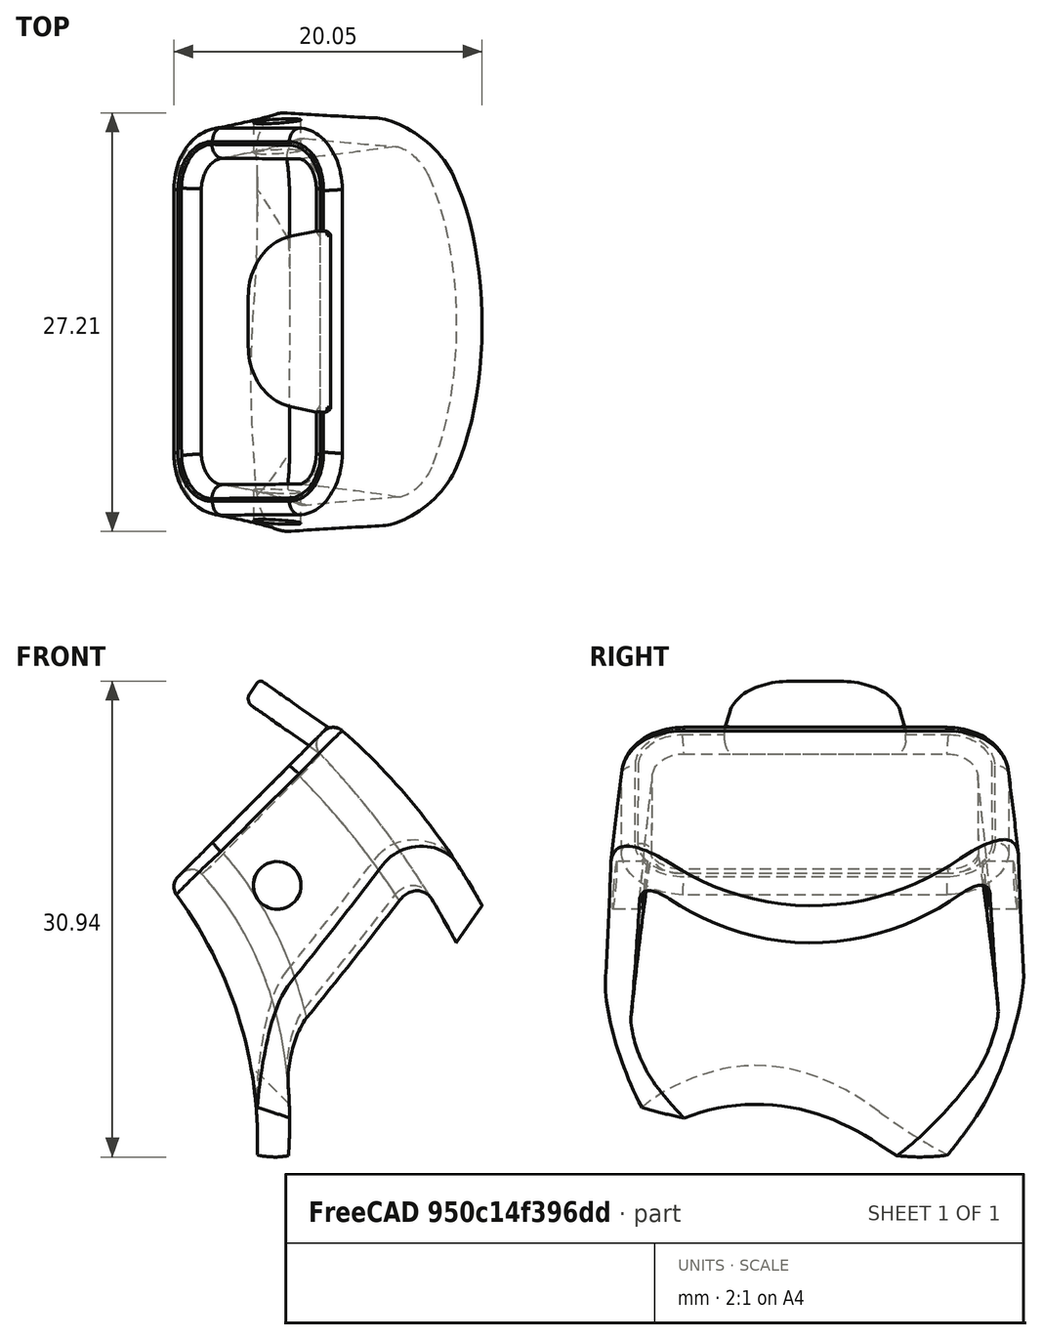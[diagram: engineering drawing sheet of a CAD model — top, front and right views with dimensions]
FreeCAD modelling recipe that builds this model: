
FCSTD DOCUMENT  (FreeCAD 0.20R28671 (Git))
Label: boquilla
License: All rights reserved
LicenseURL: http://en.wikipedia.org/wiki/All_rights_reserved
objects: TechDraw::DrawViewDimension×52, Sketcher::SketchObject×18, TechDraw::DrawViewAnnotation×11, PartDesign::Pocket×7, PartDesign::Plane×6, TechDraw::DrawLeaderLine×6, PartDesign::Fillet×4, TechDraw::DrawViewPart×4, TechDraw::DrawProjGroupItem×3, TechDraw::DrawViewSection×3, PartDesign::Pad×2, TechDraw::DrawViewBalloon×2, PartDesign::AdditivePipe×1, PartDesign::SubtractivePipe×1, TechDraw::DrawSVGTemplate×1, TechDraw::DrawProjGroup×1, TechDraw::DrawViewClip×1, TechDraw::DrawViewSymbol×1, PartDesign::Body×1, TechDraw::DrawPage×1
note: 55 computed .brp shape members not serialized (recipe doc carries the construction recipe); baked Part::Feature solids carry a one-line shape summary decoded from their .brp

FEATURE [Sketcher::SketchObject] Sketch
  FullyConstrained = true
  MapMode = 5
  Placement = pos=(0,0,0) rot=(1,0,0;1.5708rad)
  Support = -> [XZ_Plane]
  sketch-geometry (4):
    g0: ArcOfCircle CenterX=0 CenterY=-24.7487 CenterZ=0 NormalX=0 NormalY=0 NormalZ=1 AngleXU=0 Radius=35 StartAngle=0 EndAngle=0.785398
    g1: LineSegment StartX=35 StartY=-24.7487 StartZ=0 EndX=35 EndY=-62 EndZ=0
    g2: LineSegment StartX=35 StartY=-24.7487 StartZ=0 EndX=0 EndY=-24.7487 EndZ=0
    g3: LineSegment StartX=0 StartY=-24.7487 StartZ=0 EndX=24.7487 EndY=0 EndZ=0
  constraints (11):
    c: Vertical(g1)
    c: Tangent(g1,g0) = 1.5708
    c: Radius(g0) = 35
    c: DistanceY(g1,g0) = 62
    c: Vertical(g0,g-1)
    c: Horizontal(g0,g-1)
    c: Coincident(g2,g0)
    c: Coincident(g2,g0)
    c: Coincident(g3,g0)
    c: Coincident(g3,g0)
    c: Angle(g2,g3) = 0.785398
FEATURE [PartDesign::Plane] DatumPlane
  Length = 66.6467
  MapMode = 7
  Placement = pos=(24.7487,0,-1.5365e-12) rot=(0.678598,0.678598,0.281085;2.59356rad)
  ResizeMode = 0
  Support = -> [Sketch]
  Width = 155.203
FEATURE [Sketcher::SketchObject] Sketch001
  FullyConstrained = true
  MapMode = 5
  Placement = pos=(24.7487,0,-1.5365e-12) rot=(0.678598,0.678598,0.281085;2.59356rad)
  Support = -> [DatumPlane]
  sketch-geometry (10):
    g0: LineSegment StartX=-8.5 StartY=7.5 StartZ=0 EndX=8.5 EndY=7.5 EndZ=0
    g1: LineSegment StartX=12.5 StartY=3.5 StartZ=0 EndX=12.5 EndY=-3.5 EndZ=0
    g2: LineSegment StartX=8.5 StartY=-7.5 StartZ=0 EndX=-8.5 EndY=-7.5 EndZ=0
    g3: LineSegment StartX=-12.5 StartY=-3.5 StartZ=0 EndX=-12.5 EndY=3.5 EndZ=0
    g4: LineSegment StartX=0 StartY=0 StartZ=0 EndX=8.5 EndY=3.5 EndZ=0
    g5: LineSegment StartX=0 StartY=0 StartZ=0 EndX=-8.5 EndY=-3.5 EndZ=0
    g6: ArcOfCircle CenterX=-8.5 CenterY=3.5 CenterZ=0 NormalX=0 NormalY=0 NormalZ=1 AngleXU=0 Radius=4 StartAngle=1.5708 EndAngle=3.14159
    g7: ArcOfCircle CenterX=-8.5 CenterY=-3.5 CenterZ=0 NormalX=0 NormalY=0 NormalZ=1 AngleXU=0 Radius=4 StartAngle=3.14159 EndAngle=4.71239
    g8: ArcOfCircle CenterX=8.5 CenterY=-3.5 CenterZ=0 NormalX=0 NormalY=0 NormalZ=1 AngleXU=0 Radius=4 StartAngle=4.71239 EndAngle=6.28319
    g9: ArcOfCircle CenterX=8.5 CenterY=3.5 CenterZ=0 NormalX=0 NormalY=0 NormalZ=1 AngleXU=0 Radius=4 StartAngle=0 EndAngle=1.5708
  constraints (24):
    c: Horizontal(g0)
    c: Horizontal(g2)
    c: Vertical(g1)
    c: Vertical(g3)
    c: Coincident(g4,g-1)
    c: Coincident(g5,g-1)
    c: Equal(g5,g4)
    c: Tangent(g0,g6) = 1.5708
    c: Tangent(g3,g6) = 1.5708
    c: Tangent(g3,g7) = 1.5708
    c: Tangent(g2,g7) = 1.5708
    c: Tangent(g2,g8) = 1.5708
    c: Tangent(g1,g8) = 1.5708
    c: Tangent(g1,g9) = 1.5708
    c: Tangent(g0,g9) = 1.5708
    c: Coincident(g4,g9)
    c: Coincident(g5,g7)
    c: Equal(g9,g6)
    c: Equal(g6,g7)
    c: Equal(g7,g8)
    c: DistanceY(g2,g0) = 15
    c: DistanceX(g3,g1) = 25
    c: Radius(g7) = 4
    c: Parallel(g4,g5)
FEATURE [PartDesign::Plane] DatumPlane001
  Length = 111.467
  MapMode = 7
  Placement = pos=(35,5.5e-15,-24.7487) rot=(0,0,1;0rad)
  ResizeMode = 0
  Support = -> [Sketch]
  Width = 63.9644
FEATURE [Sketcher::SketchObject] Sketch002
  FullyConstrained = true
  MapMode = 5
  Placement = pos=(35,5.5e-15,-24.7487) rot=(0,0,1;0rad)
  Support = -> [DatumPlane001]
  sketch-geometry (10):
    g0: LineSegment StartX=-6 StartY=15 StartZ=0 EndX=6 EndY=15 EndZ=0
    g1: LineSegment StartX=10 StartY=11 StartZ=0 EndX=10 EndY=-11 EndZ=0
    g2: LineSegment StartX=6 StartY=-15 StartZ=0 EndX=-6 EndY=-15 EndZ=0
    g3: LineSegment StartX=-10 StartY=-11 StartZ=0 EndX=-10 EndY=11 EndZ=0
    g4: ArcOfCircle CenterX=-6 CenterY=11 CenterZ=0 NormalX=0 NormalY=0 NormalZ=1 AngleXU=0 Radius=4 StartAngle=1.5708 EndAngle=3.14159
    g5: ArcOfCircle CenterX=6 CenterY=11 CenterZ=0 NormalX=0 NormalY=0 NormalZ=1 AngleXU=0 Radius=4 StartAngle=0 EndAngle=1.5708
    g6: ArcOfCircle CenterX=-6 CenterY=-11 CenterZ=0 NormalX=0 NormalY=0 NormalZ=1 AngleXU=0 Radius=4 StartAngle=3.14159 EndAngle=4.71239
    g7: ArcOfCircle CenterX=6 CenterY=-11 CenterZ=0 NormalX=0 NormalY=0 NormalZ=1 AngleXU=0 Radius=4 StartAngle=4.71239 EndAngle=6.28319
    g8: LineSegment StartX=-6 StartY=11 StartZ=0 EndX=0 EndY=0 EndZ=0
    g9: LineSegment StartX=0 StartY=0 StartZ=0 EndX=6 EndY=-11 EndZ=0
  constraints (24):
    c: Horizontal(g0)
    c: Horizontal(g2)
    c: Vertical(g1)
    c: Vertical(g3)
    c: Tangent(g0,g4) = 1.5708
    c: Tangent(g3,g4) = 1.5708
    c: Tangent(g0,g5) = 1.5708
    c: Tangent(g1,g5) = 1.5708
    c: Tangent(g3,g6) = 1.5708
    c: Tangent(g2,g6) = 1.5708
    c: Tangent(g2,g7) = 1.5708
    c: Tangent(g1,g7) = 1.5708
    c: Equal(g4,g5)
    c: Equal(g5,g6)
    c: Equal(g6,g7)
    c: Radius(g6) = 4
    c: DistanceX(g3,g1) = 20
    c: DistanceY(g2,g0) = 30
    c: Coincident(g8,g4)
    c: Coincident(g8,g-1)
    c: Coincident(g9,g-1)
    c: Coincident(g9,g7)
    c: Parallel(g9,g8)
    c: Equal(g9,g8)
FEATURE [PartDesign::Plane] DatumPlane002
  Length = 111.467
  MapMode = 7
  Placement = pos=(35,1.38e-14,-62) rot=(0,0,1;0rad)
  ResizeMode = 0
  Support = -> [Sketch]
  Width = 63.9644
FEATURE [Sketcher::SketchObject] Sketch003
  FullyConstrained = true
  MapMode = 5
  Placement = pos=(35,1.38e-14,-62) rot=(0,0,1;0rad)
  Support = -> [DatumPlane002]
  sketch-geometry (10):
    g0: LineSegment StartX=8.5 StartY=17.5 StartZ=0 EndX=-8.5 EndY=17.5 EndZ=0
    g1: LineSegment StartX=-12.5 StartY=13.5 StartZ=0 EndX=-12.5 EndY=-13.5 EndZ=0
    g2: LineSegment StartX=-8.5 StartY=-17.5 StartZ=0 EndX=8.5 EndY=-17.5 EndZ=0
    g3: LineSegment StartX=12.5 StartY=-13.5 StartZ=0 EndX=12.5 EndY=13.5 EndZ=0
    g4: ArcOfCircle CenterX=8.5 CenterY=13.5 CenterZ=0 NormalX=0 NormalY=0 NormalZ=1 AngleXU=0 Radius=4 StartAngle=-7.19e-14 EndAngle=1.5708
    g5: ArcOfCircle CenterX=8.5 CenterY=-13.5 CenterZ=0 NormalX=0 NormalY=0 NormalZ=1 AngleXU=0 Radius=4 StartAngle=4.71239 EndAngle=6.28319
    g6: ArcOfCircle CenterX=-8.5 CenterY=-13.5 CenterZ=0 NormalX=0 NormalY=0 NormalZ=1 AngleXU=0 Radius=4 StartAngle=3.14159 EndAngle=4.71239
    g7: ArcOfCircle CenterX=-8.5 CenterY=13.5 CenterZ=0 NormalX=0 NormalY=0 NormalZ=1 AngleXU=0 Radius=4 StartAngle=1.5708 EndAngle=3.14159
    g8: LineSegment StartX=-8.5 StartY=13.5 StartZ=0 EndX=0 EndY=0 EndZ=0
    g9: LineSegment StartX=0 StartY=0 StartZ=0 EndX=8.5 EndY=-13.5 EndZ=0
  constraints (24):
    c: Horizontal(g0)
    c: Horizontal(g2)
    c: Vertical(g1)
    c: Vertical(g3)
    c: Tangent(g3,g4) = -1.5708
    c: Tangent(g0,g4) = -1.5708
    c: Tangent(g3,g5) = -1.5708
    c: Tangent(g2,g5) = -1.5708
    c: Tangent(g2,g6) = -1.5708
    c: Tangent(g1,g6) = -1.5708
    c: Tangent(g1,g7) = -1.5708
    c: Tangent(g0,g7) = -1.5708
    c: Equal(g5,g4)
    c: Equal(g4,g7)
    c: Equal(g7,g6)
    c: Radius(g6) = 4
    c: DistanceX(g1,g3) = 25
    c: DistanceY(g2,g0) = 35
    c: Coincident(g8,g7)
    c: Coincident(g8,g-1)
    c: Coincident(g9,g-1)
    c: Coincident(g9,g5)
    c: Equal(g8,g9)
    c: Parallel(g9,g8)
FEATURE [PartDesign::AdditivePipe] AdditivePipe
  AuxilleryCurvelinear = true
  AuxillerySpineTangent = false
  Binormal = (0,0,0)
  Mode = 0
  Placement = pos=(24.7487,0,-1.537e-12) rot=(0.678598,0.678598,0.281085;2.59356rad)
  Profile = -> Sketch001
  Sections = -> [Sketch002,Sketch003]
  Spine = -> Sketch
  SpineTangent = false
  Transformation = 1
  Transition = 0
FEATURE [Sketcher::SketchObject] Sketch004
  ExternalGeometry = -> [AdditivePipe]
  FullyConstrained = true
  MapMode = 5
  Placement = pos=(24.7487,-8.1e-15,-62) rot=(0.707107,0.707107,0;3.14159rad)
  Support = -> [AdditivePipe]
  sketch-geometry (24):
    g0: LineSegment StartX=-13.5 StartY=22.7513 StartZ=0 EndX=13.5 EndY=-2.24874 EndZ=0
    g1: LineSegment StartX=13.5 StartY=22.7513 StartZ=0 EndX=-13.5 EndY=-2.24874 EndZ=0
    g2: GeomPoint X=2.51e-14 Y=10.2513 Z=0
    g3: LineSegment StartX=-12.5 StartY=20.7513 StartZ=0 EndX=12.5 EndY=20.7513 EndZ=0
    g4: LineSegment StartX=15.5 StartY=17.7513 StartZ=0 EndX=15.5 EndY=5 EndZ=0
    g5: LineSegment StartX=12.5 StartY=2 StartZ=0 EndX=-12.5 EndY=2 EndZ=0
    g6: LineSegment StartX=-15.5 StartY=5 StartZ=0 EndX=-15.5 EndY=17.7513 EndZ=0
    g7: ArcOfCircle CenterX=-12.5 CenterY=17.7513 CenterZ=0 NormalX=0 NormalY=0 NormalZ=1 AngleXU=0 Radius=3 StartAngle=1.5708 EndAngle=3.14159
    g8: ArcOfCircle CenterX=12.5 CenterY=17.7513 CenterZ=0 NormalX=0 NormalY=0 NormalZ=1 AngleXU=0 Radius=3 StartAngle=2e-16 EndAngle=1.5708
    g9: ArcOfCircle CenterX=12.5 CenterY=5 CenterZ=0 NormalX=0 NormalY=0 NormalZ=1 AngleXU=0 Radius=3 StartAngle=4.71239 EndAngle=6.28319
    g10: ArcOfCircle CenterX=-12.5 CenterY=5 CenterZ=0 NormalX=0 NormalY=0 NormalZ=1 AngleXU=0 Radius=3 StartAngle=3.14159 EndAngle=4.71239
    g11: LineSegment StartX=-12.5 StartY=20.7513 StartZ=0 EndX=-12.5 EndY=22.7513 EndZ=0
    g12: LineSegment StartX=-12.5 StartY=2 StartZ=0 EndX=-12.5 EndY=0 EndZ=0
    g13: LineSegment StartX=-15.5 StartY=5 StartZ=0 EndX=-17.5 EndY=5 EndZ=0
    g14: LineSegment StartX=15.5 StartY=5 StartZ=0 EndX=17.5 EndY=5 EndZ=0
    g15: LineSegment StartX=-19.5 StartY=24.7513 StartZ=0 EndX=19.5 EndY=24.7513 EndZ=0
    g16: LineSegment StartX=19.5 StartY=24.7513 StartZ=0 EndX=19.5 EndY=-4.24874 EndZ=0
    g17: LineSegment StartX=19.5 StartY=-4.24874 StartZ=0 EndX=-19.5 EndY=-4.24874 EndZ=0
    g18: LineSegment StartX=-19.5 StartY=-4.24874 StartZ=0 EndX=-19.5 EndY=24.7513 EndZ=0
    g19: LineSegment StartX=-19.5 StartY=24.7513 StartZ=0 EndX=-17.5 EndY=18.7513 EndZ=0
    g20: LineSegment StartX=-19.5 StartY=24.7513 StartZ=0 EndX=-13.5 EndY=22.7513 EndZ=0
    g21: LineSegment StartX=19.5 StartY=-4.24874 StartZ=0 EndX=13.5 EndY=-2.24874 EndZ=0
    g22: LineSegment StartX=19.5 StartY=-4.24874 StartZ=0 EndX=17.5 EndY=1.75126 EndZ=0
    g23: LineSegment StartX=17.5 StartY=18.7513 StartZ=0 EndX=19.5 EndY=18.7513 EndZ=0
  constraints (61):
    c: Coincident(g0,g-3)
    c: Coincident(g0,g-4)
    c: Coincident(g1,g-5)
    c: Coincident(g1,g-6)
    c: PointOnObject(g2,g0)
    c: PointOnObject(g2,g1)
    c: Horizontal(g3)
    c: Horizontal(g5)
    c: Vertical(g4)
    c: Vertical(g6)
    c: Tangent(g3,g7) = 1.5708
    c: Tangent(g6,g7) = 1.5708
    c: Tangent(g3,g8) = 1.5708
    c: Tangent(g4,g8) = 1.5708
    c: Tangent(g4,g9) = 1.5708
    c: Tangent(g5,g9) = 1.5708
    c: Tangent(g5,g10) = 1.5708
    c: Tangent(g6,g10) = 1.5708
    c: Equal(g7,g8)
    c: Equal(g8,g10)
    c: Equal(g10,g9)
    c: Radius(g9) = 3
    c: DistanceY(g3,g1) = 2
    c: Coincident(g11,g3)
    c: Vertical(g11)
    c: Horizontal(g11,g0)
    c: Coincident(g12,g5)
    c: PointOnObject(g12,g-1)
    c: Vertical(g12)
    c: Equal(g12,g11)
    c: Coincident(g13,g6)
    c: Horizontal(g13)
    c: Coincident(g14,g4)
    c: Horizontal(g14)
    c: Vertical(g-6,g13)
    c: Vertical(g-4,g14)
    c: Equal(g12,g13)
    c: Equal(g13,g14)
    c: Coincident(g15,g16)
    c: Coincident(g16,g17)
    c: Coincident(g17,g18)
    c: Coincident(g18,g15)
    c: Horizontal(g15)
    c: Horizontal(g17)
    c: Vertical(g16)
    c: Vertical(g18)
    c: Coincident(g19,g15)
    c: Coincident(g19,g-3)
    c: Coincident(g20,g15)
    c: Coincident(g20,g0)
    c: Coincident(g21,g16)
    c: Coincident(g21,g0)
    c: Coincident(g22,g16)
    c: Coincident(g22,g-4)
    c: Equal(g22,g21)
    c: Equal(g21,g19)
    c: Equal(g19,g20)
    c: Coincident(g23,g-5)
    c: PointOnObject(g23,g16)
    c: Horizontal(g23)
    c: Equal(g11,g23)
FEATURE [PartDesign::Pocket] Pocket
  BaseFeature = -> AdditivePipe
  Direction = (-1e-16,0,1)
  Length = 2
  Length2 = 100
  Placement = pos=(24.7487,0,-1.537e-12) rot=(0.678598,0.678598,0.281085;2.59356rad)
  Profile = -> Sketch004
  Type = 0
FEATURE [Sketcher::SketchObject] Sketch006
  FullyConstrained = true
  MapMode = 5
  Placement = pos=(24.7487,0,-1.5365e-12) rot=(0.678598,0.678598,0.281085;2.59356rad)
  Support = -> [DatumPlane]
  sketch-geometry (10):
    g0: LineSegment StartX=-8.5 StartY=5.5 StartZ=0 EndX=8.5 EndY=5.5 EndZ=0
    g1: LineSegment StartX=10.5 StartY=3.5 StartZ=0 EndX=10.5 EndY=-3.5 EndZ=0
    g2: LineSegment StartX=8.5 StartY=-5.5 StartZ=0 EndX=-8.5 EndY=-5.5 EndZ=0
    g3: LineSegment StartX=-10.5 StartY=-3.5 StartZ=0 EndX=-10.5 EndY=3.5 EndZ=0
    g4: ArcOfCircle CenterX=-8.5 CenterY=3.5 CenterZ=0 NormalX=0 NormalY=0 NormalZ=1 AngleXU=0 Radius=2 StartAngle=1.5708 EndAngle=3.14159
    g5: ArcOfCircle CenterX=-8.5 CenterY=-3.5 CenterZ=0 NormalX=0 NormalY=0 NormalZ=1 AngleXU=0 Radius=2 StartAngle=3.14159 EndAngle=4.71239
    g6: ArcOfCircle CenterX=8.5 CenterY=-3.5 CenterZ=0 NormalX=0 NormalY=0 NormalZ=1 AngleXU=0 Radius=2 StartAngle=4.71239 EndAngle=6.28319
    g7: ArcOfCircle CenterX=8.5 CenterY=3.5 CenterZ=0 NormalX=0 NormalY=0 NormalZ=1 AngleXU=0 Radius=2 StartAngle=0 EndAngle=1.5708
    g8: LineSegment StartX=-8.5 StartY=3.5 StartZ=0 EndX=0 EndY=0 EndZ=0
    g9: LineSegment StartX=0 StartY=0 StartZ=0 EndX=8.5 EndY=-3.5 EndZ=0
  constraints (24):
    c: Horizontal(g0)
    c: Horizontal(g2)
    c: Vertical(g1)
    c: Vertical(g3)
    c: Tangent(g0,g4) = 1.5708
    c: Tangent(g3,g4) = 1.5708
    c: Tangent(g3,g5) = 1.5708
    c: Tangent(g2,g5) = 1.5708
    c: Tangent(g2,g6) = 1.5708
    c: Tangent(g1,g6) = 1.5708
    c: Tangent(g1,g7) = 1.5708
    c: Tangent(g0,g7) = 1.5708
    c: Equal(g4,g5)
    c: Equal(g5,g6)
    c: Equal(g6,g7)
    c: Radius(g4) = 2
    c: Coincident(g8,g4)
    c: Coincident(g8,g-1)
    c: Coincident(g9,g-1)
    c: Coincident(g9,g6)
    c: Equal(g9,g8)
    c: Parallel(g8,g9)
    c: DistanceY(g2,g0) = 11
    c: DistanceX(g3,g1) = 21
FEATURE [Sketcher::SketchObject] Sketch007
  FullyConstrained = true
  MapMode = 5
  Placement = pos=(35,5.5e-15,-24.7487) rot=(0,0,1;0rad)
  Support = -> [DatumPlane001]
  sketch-geometry (10):
    g0: LineSegment StartX=-6 StartY=13 StartZ=0 EndX=6 EndY=13 EndZ=0
    g1: LineSegment StartX=8 StartY=11 StartZ=0 EndX=8 EndY=-11 EndZ=0
    g2: LineSegment StartX=6 StartY=-13 StartZ=0 EndX=-6 EndY=-13 EndZ=0
    g3: LineSegment StartX=-8 StartY=-11 StartZ=0 EndX=-8 EndY=11 EndZ=0
    g4: ArcOfCircle CenterX=6 CenterY=11 CenterZ=0 NormalX=0 NormalY=0 NormalZ=1 AngleXU=0 Radius=2 StartAngle=8.55e-14 EndAngle=1.5708
    g5: ArcOfCircle CenterX=-6 CenterY=11 CenterZ=0 NormalX=0 NormalY=0 NormalZ=1 AngleXU=0 Radius=2 StartAngle=1.5708 EndAngle=3.14159
    g6: ArcOfCircle CenterX=-6 CenterY=-11 CenterZ=0 NormalX=0 NormalY=0 NormalZ=1 AngleXU=0 Radius=2 StartAngle=3.14159 EndAngle=4.71239
    g7: ArcOfCircle CenterX=6 CenterY=-11 CenterZ=0 NormalX=0 NormalY=0 NormalZ=1 AngleXU=0 Radius=2 StartAngle=4.71239 EndAngle=6.28319
    g8: LineSegment StartX=-6 StartY=11 StartZ=0 EndX=0 EndY=0 EndZ=0
    g9: LineSegment StartX=0 StartY=0 StartZ=0 EndX=6 EndY=-11 EndZ=0
  constraints (24):
    c: Horizontal(g0)
    c: Horizontal(g2)
    c: Vertical(g1)
    c: Vertical(g3)
    c: Tangent(g1,g4) = 1.5708
    c: Tangent(g0,g4) = 1.5708
    c: Tangent(g0,g5) = 1.5708
    c: Tangent(g3,g5) = 1.5708
    c: Tangent(g3,g6) = 1.5708
    c: Tangent(g2,g6) = 1.5708
    c: Tangent(g2,g7) = 1.5708
    c: Tangent(g1,g7) = 1.5708
    c: Equal(g4,g5)
    c: Equal(g5,g6)
    c: Equal(g6,g7)
    c: Radius(g4) = 2
    c: Coincident(g8,g5)
    c: Coincident(g8,g-1)
    c: Coincident(g9,g-1)
    c: Coincident(g9,g7)
    c: Equal(g8,g9)
    c: Parallel(g8,g9)
    c: DistanceX(g3,g1) = 16
    c: DistanceY(g2,g0) = 26
FEATURE [PartDesign::Plane] DatumPlane003
  AttachmentOffset = pos=(0,0,-2) rot=(0,0,1;0rad)
  Length = 63.9644
  MapMode = 5
  Placement = pos=(24.7487,0,-58) rot=(0.707107,0.707107,0;3.14159rad)
  ResizeMode = 0
  Support = -> [Pocket]
  Width = 111.467
FEATURE [Sketcher::SketchObject] Sketch008
  ExternalGeometry = -> [Sketch]
  FullyConstrained = true
  MapMode = 5
  Placement = pos=(24.7487,0,-58) rot=(0.707107,0.707107,0;3.14159rad)
  Support = -> [DatumPlane003]
  sketch-geometry (10):
    g0: LineSegment StartX=-13.5 StartY=20.7513 StartZ=0 EndX=13.5 EndY=20.7513 EndZ=0
    g1: LineSegment StartX=15.5 StartY=18.7513 StartZ=0 EndX=15.5 EndY=1.75126 EndZ=0
    g2: LineSegment StartX=13.5 StartY=-0.248737 StartZ=0 EndX=-13.5 EndY=-0.248737 EndZ=0
    g3: LineSegment StartX=-15.5 StartY=1.75126 StartZ=0 EndX=-15.5 EndY=18.7513 EndZ=0
    g4: ArcOfCircle CenterX=-13.5 CenterY=18.7513 CenterZ=0 NormalX=0 NormalY=0 NormalZ=1 AngleXU=0 Radius=2 StartAngle=1.5708 EndAngle=3.14159
    g5: ArcOfCircle CenterX=13.5 CenterY=18.7513 CenterZ=0 NormalX=0 NormalY=0 NormalZ=1 AngleXU=0 Radius=2 StartAngle=8.58e-14 EndAngle=1.5708
    g6: ArcOfCircle CenterX=13.5 CenterY=1.75126 CenterZ=0 NormalX=0 NormalY=0 NormalZ=1 AngleXU=0 Radius=2 StartAngle=4.71239 EndAngle=6.28319
    g7: ArcOfCircle CenterX=-13.5 CenterY=1.75126 CenterZ=0 NormalX=0 NormalY=0 NormalZ=1 AngleXU=0 Radius=2 StartAngle=3.14159 EndAngle=4.71239
    g8: LineSegment StartX=-13.5 StartY=18.7513 StartZ=0 EndX=3.55e-14 EndY=10.2513 EndZ=0
    g9: LineSegment StartX=3.55e-14 StartY=10.2513 StartZ=0 EndX=13.5 EndY=1.75126 EndZ=0
  constraints (24):
    c: Horizontal(g0)
    c: Horizontal(g2)
    c: Vertical(g1)
    c: Vertical(g3)
    c: Tangent(g0,g4) = 1.5708
    c: Tangent(g3,g4) = 1.5708
    c: Tangent(g0,g5) = 1.5708
    c: Tangent(g1,g5) = 1.5708
    c: Tangent(g1,g6) = 1.5708
    c: Tangent(g2,g6) = 1.5708
    c: Tangent(g2,g7) = 1.5708
    c: Tangent(g3,g7) = 1.5708
    c: Equal(g6,g5)
    c: Equal(g5,g4)
    c: Equal(g4,g7)
    c: Radius(g5) = 2
    c: Coincident(g8,g4)
    c: Coincident(g8,g-3)
    c: Coincident(g9,g8)
    c: Coincident(g9,g6)
    c: Parallel(g9,g8)
    c: Equal(g9,g8)
    c: DistanceX(g3,g1) = 31
    c: DistanceY(g2,g0) = 21
FEATURE [Sketcher::SketchObject] Sketch009
  ExternalGeometry = -> [Sketch,Sketch008]
  FullyConstrained = true
  MapMode = 5
  Placement = pos=(0,0,0) rot=(1,0,0;1.5708rad)
  Support = -> [XZ_Plane]
  sketch-geometry (2):
    g0: ArcOfCircle CenterX=3.3e-15 CenterY=-24.7487 CenterZ=0 NormalX=0 NormalY=0 NormalZ=1 AngleXU=0 Radius=35 StartAngle=0 EndAngle=0.785398
    g1: LineSegment StartX=35 StartY=-24.7487 StartZ=0 EndX=35 EndY=-58 EndZ=0
  constraints (6):
    c: Coincident(g0,g-3)
    c: Coincident(g0,g-4)
    c: Tangent(g0,g-3)
    c: Coincident(g1,g0)
    c: PointOnObject(g1,g-4)
    c: Horizontal(g1,g-5)
FEATURE [PartDesign::SubtractivePipe] SubtractivePipe
  AuxilleryCurvelinear = true
  AuxillerySpineTangent = false
  BaseFeature = -> Pocket
  Binormal = (0,0,0)
  Mode = 1
  Placement = pos=(24.7487,0,-1.537e-12) rot=(0.678598,0.678598,0.281085;2.59356rad)
  Profile = -> Sketch006
  Sections = -> [Sketch007,Sketch008]
  Spine = -> Sketch009
  SpineTangent = false
  Transformation = 1
  Transition = 0
FEATURE [PartDesign::Plane] DatumPlane004
  AttachmentOffset = pos=(0,0,35) rot=(0,0,1;0rad)
  Length = 64.0318
  MapMode = 5
  Placement = pos=(35,-7.8e-15,7.8e-15) rot=(0.57735,0.57735,0.57735;2.0944rad)
  ResizeMode = 0
  Support = -> [YZ_Plane]
  Width = 112.478
FEATURE [Sketcher::SketchObject] Sketch010
  ExternalGeometry = -> [Sketch008]
  FullyConstrained = true
  MapMode = 5
  Placement = pos=(35,-7.8e-15,7.8e-15) rot=(0.57735,0.57735,0.57735;2.0944rad)
  Support = -> [DatumPlane004]
  sketch-geometry (6):
    g0: LineSegment StartX=-9.4 StartY=-58 StartZ=0 EndX=9.4 EndY=-58 EndZ=0
    g1: LineSegment StartX=9.4 StartY=-58 StartZ=0 EndX=9.4 EndY=-29.5 EndZ=0
    g2: LineSegment StartX=9.4 StartY=-29.5 StartZ=0 EndX=-9.4 EndY=-29.5 EndZ=0
    g3: LineSegment StartX=-9.4 StartY=-29.5 StartZ=0 EndX=-9.4 EndY=-58 EndZ=0
    g4: LineSegment StartX=-13.5 StartY=-58 StartZ=0 EndX=-9.4 EndY=-58 EndZ=0
    g5: LineSegment StartX=13.5 StartY=-58 StartZ=0 EndX=9.4 EndY=-58 EndZ=0
  constraints (16):
    c: Coincident(g0,g1)
    c: Coincident(g1,g2)
    c: Coincident(g2,g3)
    c: Coincident(g3,g0)
    c: Horizontal(g0)
    c: Horizontal(g2)
    c: Vertical(g1)
    c: Vertical(g3)
    c: PointOnObject(g0,g-3)
    c: DistanceX(g0,g0) = 18.8
    c: DistanceY(g0,g1) = 28.5
    c: Coincident(g4,g-3)
    c: Coincident(g5,g-3)
    c: Equal(g5,g4)
    c: Coincident(g4,g0)
    c: Coincident(g5,g0)
FEATURE [PartDesign::Pocket] Pocket001
  BaseFeature = -> SubtractivePipe
  Direction = (-1,1e-16,-1e-16)
  Length = 5
  Length2 = 100
  Placement = pos=(24.7487,0,-1.537e-12) rot=(0.678598,0.678598,0.281085;2.59356rad)
  Profile = -> Sketch010
  Reversed = true
  Type = 1
FEATURE [Sketcher::SketchObject] Sketch011
  ExternalGeometry = -> [Pocket001]
  FullyConstrained = true
  MapMode = 5
  Placement = pos=(0,0,0) rot=(1,0,0;1.5708rad)
  Support = -> [XZ_Plane]
  sketch-geometry (1):
    g0: Circle CenterX=26.4454 CenterY=-5.3033 CenterZ=0 NormalX=0 NormalY=0 NormalZ=1 AngleXU=0 Radius=1.55
  constraints (3):
    c: Diameter(g0) = 3.1
    c: DistanceX(g-3,g0) = 7
    c: DistanceY(g0,g-3) = 0
FEATURE [PartDesign::Pocket] Pocket002
  BaseFeature = -> Pocket001
  Direction = (0,1,2e-16)
  Length = 5
  Length2 = 100
  Midplane = true
  Placement = pos=(24.7487,0,-1.537e-12) rot=(0.678598,0.678598,0.281085;2.59356rad)
  Profile = -> Sketch011
  Type = 1
FEATURE [PartDesign::Fillet] Fillet
  Base = -> Pocket002 [Edge79,Edge87]
  BaseFeature = -> Pocket002
  Placement = pos=(24.7487,0,-1.537e-12) rot=(0.678598,0.678598,0.281085;2.59356rad)
  Radius = 0.9
  SupportTransform = false
  UseAllEdges = false
FEATURE [Sketcher::SketchObject] Sketch012
  ExternalGeometry = -> [Sketch,Fillet]
  FullyConstrained = true
  MapMode = 5
  Placement = pos=(0,0,0) rot=(1,0,0;1.5708rad)
  Support = -> [XZ_Plane]
  sketch-geometry (1):
    g0: LineSegment StartX=29.2448 StartY=3.25778 StartZ=0 EndX=0 EndY=23.7352 EndZ=0
  constraints (3):
    c: Angle(g0,g-3) = 2.18166
    c: Vertical(g-1,g0)
    c: Coincident(g0,g-6)
FEATURE [PartDesign::Plane] DatumPlane005
  Length = 66.5128
  MapMode = 13
  Placement = pos=(19.4965,2.85578,10.0836) rot=(0.287968,0.287968,0.913318;1.66134rad)
  ResizeMode = 0
  Support = -> [Sketch012,Fillet]
  Width = 152.849
FEATURE [Sketcher::SketchObject] Sketch013
  ExternalGeometry = -> [Sketch012]
  FullyConstrained = true
  MapMode = 5
  Placement = pos=(19.4965,2.85578,10.0836) rot=(0.287968,0.287968,0.913318;1.66134rad)
  Support = -> [DatumPlane005]
  sketch-geometry (6):
    g0: LineSegment StartX=-8.85578 StartY=-11.9004 StartZ=0 EndX=-7.85578 EndY=-5.90042 EndZ=0
    g1: LineSegment StartX=-7.85578 StartY=-5.90042 StartZ=0 EndX=2.14422 EndY=-5.90042 EndZ=0
    g2: LineSegment StartX=2.14422 StartY=-5.90042 StartZ=0 EndX=3.14422 EndY=-11.9004 EndZ=0
    g3: LineSegment StartX=-8.85578 StartY=-11.9004 StartZ=0 EndX=3.14422 EndY=-11.9004 EndZ=0
    g4: LineSegment StartX=-2.85578 StartY=-11.9004 StartZ=0 EndX=-8.85578 EndY=-11.9004 EndZ=0
    g5: LineSegment StartX=-2.85578 StartY=-11.9004 StartZ=0 EndX=3.14422 EndY=-11.9004 EndZ=0
  constraints (16):
    c: Coincident(g1,g0)
    c: Horizontal(g1)
    c: Coincident(g2,g1)
    c: Coincident(g3,g0)
    c: Coincident(g3,g2)
    c: Horizontal(g3)
    c: Equal(g4,g5)
    c: Coincident(g4,g0)
    c: Coincident(g5,g2)
    c: Equal(g0,g2)
    c: DistanceY(g2,g1) = 6
    c: DistanceX(g3,g3) = 12
    c: DistanceX(g1,g1) = 10
    c: Coincident(g5,g4)
    c: Horizontal(g5)
    c: Coincident(g4,g-3)
FEATURE [PartDesign::Pad] Pad
  BaseFeature = -> Fillet
  Direction = (0.573576,1.4e-15,0.819152)
  Length = 1.7
  Length2 = 100
  Placement = pos=(24.7487,0,-1.537e-12) rot=(0.678598,0.678598,0.281085;2.59356rad)
  Profile = -> Sketch013
  ReferenceAxis = -> Sketch013 [N_Axis]
  Type = 0
FEATURE [PartDesign::Fillet] Fillet001
  Base = -> Pad [Edge104,Edge85]
  BaseFeature = -> Pad
  Placement = pos=(24.7487,0,-1.537e-12) rot=(0.678598,0.678598,0.281085;2.59356rad)
  Radius = 4
  SupportTransform = false
  UseAllEdges = false
FEATURE [PartDesign::Fillet] Fillet002
  Base = -> Fillet001 [Edge1,Edge7,Edge11,Edge10,Edge8]
  BaseFeature = -> Fillet001
  Placement = pos=(24.7487,0,-1.537e-12) rot=(0.678598,0.678598,0.281085;2.59356rad)
  Radius = 0.6
  SupportTransform = false
  UseAllEdges = false
FEATURE [PartDesign::Fillet] Fillet003
  Base = -> Fillet002 [Face4]
  BaseFeature = -> Fillet002
  Placement = pos=(24.7487,0,-1.537e-12) rot=(0.678598,0.678598,0.281085;2.59356rad)
  Radius = 0.3
  SupportTransform = false
  UseAllEdges = false
FEATURE [Sketcher::SketchObject] Sketch014
  ExternalGeometry = -> [Fillet003]
  FullyConstrained = true
  MapMode = 5
  Placement = pos=(24.7487,-8.1e-15,-62) rot=(0.707107,0.707107,0;3.14159rad)
  Support = -> [Fillet003]
  sketch-geometry (1):
    g0: Circle CenterX=-8.5 CenterY=7 CenterZ=0 NormalX=0 NormalY=0 NormalZ=1 AngleXU=0 Radius=2.5
  constraints (3):
    c: Diameter(g0) = 5
    c: DistanceX(g-4,g0) = 4
    c: DistanceY(g-4,g0) = 5
FEATURE [PartDesign::Pocket] Pocket003
  BaseFeature = -> Fillet003
  Direction = (-7e-16,1e-16,1)
  Length = 0
  Length2 = 100
  Placement = pos=(24.7487,0,-1.537e-12) rot=(0.678598,0.678598,0.281085;2.59356rad)
  Profile = -> Sketch014
  Type = 3
  UpToFace = -> Fillet003 [Face65]
FEATURE [Sketcher::SketchObject] Sketch015
  ExternalGeometry = -> [Pocket003]
  FullyConstrained = true
  MapMode = 5
  Placement = pos=(35,-7.8e-15,7.8e-15) rot=(0.57735,0.57735,0.57735;2.0944rad)
  Support = -> [DatumPlane004]
  sketch-geometry (1):
    g0: Circle CenterX=0 CenterY=-44 CenterZ=0 NormalX=0 NormalY=0 NormalZ=1 AngleXU=0 Radius=5
  constraints (3):
    c: PointOnObject(g0,g-2)
    c: Diameter(g0) = 10
    c: DistanceY(g-3,g0) = 18
FEATURE [PartDesign::Pocket] Pocket004
  BaseFeature = -> Pocket003
  Direction = (-1,1e-16,-1e-16)
  Length = 5
  Length2 = 100
  Placement = pos=(24.7487,0,-1.537e-12) rot=(0.678598,0.678598,0.281085;2.59356rad)
  Profile = -> Sketch015
  Type = 1
FEATURE [Sketcher::SketchObject] Sketch016
  ExternalGeometry = -> [Pocket004]
  FullyConstrained = true
  MapMode = 5
  Placement = pos=(24.7487,-8.1e-15,-62) rot=(0.707107,0.707107,0;3.14159rad)
  Support = -> [Pocket004]
  sketch-geometry (9):
    g0: ArcOfCircle CenterX=-12.5 CenterY=17.7513 CenterZ=0 NormalX=0 NormalY=0 NormalZ=1 AngleXU=0 Radius=3 StartAngle=1.5708 EndAngle=3.14159
    g1: ArcOfCircle CenterX=12.5 CenterY=17.7513 CenterZ=0 NormalX=0 NormalY=0 NormalZ=1 AngleXU=0 Radius=3 StartAngle=8e-16 EndAngle=1.5708
    g2: ArcOfCircle CenterX=12.5 CenterY=5 CenterZ=0 NormalX=0 NormalY=0 NormalZ=1 AngleXU=0 Radius=3 StartAngle=4.71239 EndAngle=6.28319
    g3: ArcOfCircle CenterX=-12.5 CenterY=5 CenterZ=0 NormalX=0 NormalY=0 NormalZ=1 AngleXU=0 Radius=3 StartAngle=3.14159 EndAngle=4.71239
    g4: LineSegment StartX=-15.5 StartY=17.7513 StartZ=0 EndX=-15.5 EndY=5 EndZ=0
    g5: LineSegment StartX=-12.5 StartY=2 StartZ=0 EndX=12.5 EndY=2 EndZ=0
    g6: LineSegment StartX=15.5 StartY=5 StartZ=0 EndX=15.5 EndY=17.7513 EndZ=0
    g7: LineSegment StartX=12.5 StartY=20.7513 StartZ=0 EndX=-12.5 EndY=20.7513 EndZ=0
    g8: Circle CenterX=-8.5 CenterY=7 CenterZ=0 NormalX=0 NormalY=0 NormalZ=1 AngleXU=0 Radius=2.5
  constraints (18):
    c: Coincident(g4,g3)
    c: Coincident(g6,g2)
    c: Coincident(g7,g1)
    c: Coincident(g7,g0)
    c: Tangent(g4,g0) = -1.5708
    c: Tangent(g6,g1) = -1.5708
    c: Tangent(g5,g2) = -1.5708
    c: Tangent(g5,g3) = -1.5708
    c: Coincident(g-10,g3)
    c: Coincident(g-10,g2)
    c: Coincident(g-4,g2)
    c: Coincident(g-9,g3)
    c: Coincident(g-5,g1)
    c: Coincident(g0,g-8)
    c: Coincident(g0,g-7)
    c: Coincident(g1,g-6)
    c: Coincident(g-11,g8)
    c: Equal(g-11,g8)
FEATURE [PartDesign::Pad] Pad001
  BaseFeature = -> Pocket004
  Direction = (9e-16,-1e-16,-1)
  Length = 2
  Length2 = 10
  Placement = pos=(24.7487,0,-1.537e-12) rot=(0.678598,0.678598,0.281085;2.59356rad)
  Profile = -> Sketch016
  ReferenceAxis = -> Sketch016 [N_Axis]
  Type = 0
FEATURE [TechDraw::DrawSVGTemplate] Template003
  EditableTexts = AUTHOR_NAME=Daniel García García; DATE=14-04-2022; DN=10; DOCUMENT_TYPE=Plano de pieza; PN=13; REVISION=1; SCALE=1:1; SHEET=10/15; SIZE=A4; TITLELINE-1=Boquilla
  Height = 210
  Orientation = 1
  Width = 297
FEATURE [TechDraw::DrawProjGroupItem] ProjItem  label="Front"
  CoarseView = false
  Direction = (-1,0,0)
  Focus = 100
  HardHidden = false
  IsoCount = 0
  IsoHidden = false
  IsoVisible = false
  LockPosition = true
  Perspective = false
  Rotation = 0
  RotationVector = (0,-1,0)
  ScaleType = 2
  SeamHidden = false
  SeamVisible = true
  SmoothHidden = false
  SmoothVisible = true
  Source = -> [Pad001]
  Type = 0
  X = 0
  XDirection = (0,-1,0)
  Y = 0
FEATURE [TechDraw::DrawProjGroupItem] ProjItem001  label="Right"
  CoarseView = false
  Direction = (-1e-16,-1,0)
  Focus = 100
  HardHidden = false
  IsoCount = 0
  IsoHidden = false
  IsoVisible = false
  LockPosition = true
  Perspective = false
  Rotation = 0
  RotationVector = (1,0,0)
  ScaleType = 2
  SeamHidden = false
  SeamVisible = true
  SmoothHidden = false
  SmoothVisible = true
  Source = -> [Pad001]
  Type = 2
  X = -98.1887
  XDirection = (1,-1e-16,0)
  Y = 0
FEATURE [TechDraw::DrawProjGroupItem] ProjItem002  label="Rear"
  CoarseView = false
  Direction = (1,0,0)
  Focus = 100
  HardHidden = false
  IsoCount = 0
  IsoHidden = false
  IsoVisible = false
  LockPosition = true
  Perspective = false
  Rotation = 0
  RotationVector = (1,0,0)
  ScaleType = 2
  SeamHidden = false
  SeamVisible = true
  SmoothHidden = false
  SmoothVisible = true
  Source = -> [Pad001]
  Type = 3
  X = 83.712
  XDirection = (0,1,0)
  Y = 0
FEATURE [TechDraw::DrawProjGroup] ProjGroup
  Anchor = -> ProjItem
  AutoDistribute = true
  LockPosition = false
  ProjectionType = 0
  Rotation = 0
  ScaleType = 0
  Source = -> [Pad001,Sketch003]
  Views = -> [ProjItem,ProjItem001,ProjItem002]
  X = 164.554
  Y = 125.603
  spacingX = 15
  spacingY = 15
FEATURE [TechDraw::DrawViewDimension] Dimension
  AngleOverride = false
  Arbitrary = false
  ArbitraryTolerances = false
  EqualTolerance = true
  ExtensionAngle = 0
  FormatSpec = ⌀%.2w
  FormatSpecOverTolerance = %+.2w
  FormatSpecUnderTolerance = %+.2w
  Inverted = false
  LineAngle = 0
  LockPosition = false
  MeasureType = 1
  OverTolerance = 0
  References2D = -> [ProjItem]
  Rotation = 0
  ScaleType = 0
  TheoreticalExact = false
  Type = 5
  UnderTolerance = 0
  X = 23.6821
  Y = -4.52112
FEATURE [TechDraw::DrawViewDimension] Dimension001
  AngleOverride = false
  Arbitrary = false
  ArbitraryTolerances = false
  EqualTolerance = true
  ExtensionAngle = 0
  FormatSpec = %.2w
  FormatSpecOverTolerance = %+.2w
  FormatSpecUnderTolerance = %+.2w
  Inverted = false
  LineAngle = 0
  LockPosition = false
  MeasureType = 1
  OverTolerance = 0
  References2D = -> [ProjItem002]
  Rotation = 0
  ScaleType = 0
  TheoreticalExact = false
  Type = 1
  UnderTolerance = 0
  X = -31.002
  Y = 1.44388
FEATURE [TechDraw::DrawViewDimension] Dimension002
  AngleOverride = false
  Arbitrary = false
  ArbitraryTolerances = false
  EqualTolerance = true
  ExtensionAngle = 0
  FormatSpec = %.2w
  FormatSpecOverTolerance = %+.2w
  FormatSpecUnderTolerance = %+.2w
  Inverted = false
  LineAngle = 0
  LockPosition = false
  MeasureType = 1
  OverTolerance = 0
  References2D = -> [ProjItem002]
  Rotation = 0
  ScaleType = 0
  TheoreticalExact = false
  Type = 2
  UnderTolerance = 0
  X = 29.6374
  Y = -14.3132
FEATURE [TechDraw::DrawViewDimension] Dimension003
  AngleOverride = false
  Arbitrary = false
  ArbitraryTolerances = false
  EqualTolerance = true
  ExtensionAngle = 0
  FormatSpec = %.2w
  FormatSpecOverTolerance = %+.2w
  FormatSpecUnderTolerance = %+.2w
  Inverted = false
  LineAngle = 0
  LockPosition = false
  MeasureType = 1
  OverTolerance = 0
  References2D = -> [ProjItem002]
  Rotation = 0
  ScaleType = 0
  TheoreticalExact = false
  Type = 2
  UnderTolerance = 0
  X = -27.9668
  Y = -20.2714
FEATURE [TechDraw::DrawViewDimension] Dimension004
  AngleOverride = false
  Arbitrary = false
  ArbitraryTolerances = false
  EqualTolerance = true
  ExtensionAngle = 0
  FormatSpec = ⌀%.2w
  FormatSpecOverTolerance = %+.2w
  FormatSpecUnderTolerance = %+.2w
  Inverted = false
  LineAngle = 0
  LockPosition = false
  MeasureType = 1
  OverTolerance = 0
  Rotation = 0
  ScaleType = 0
  TheoreticalExact = false
  Type = 5
  UnderTolerance = 0
  X = 30.8557
  Y = 1.37573
FEATURE [TechDraw::DrawViewDimension] Dimension008
  AngleOverride = false
  Arbitrary = false
  ArbitraryTolerances = false
  EqualTolerance = true
  ExtensionAngle = 0
  FormatSpec = R%.2w
  FormatSpecOverTolerance = %+.2w
  FormatSpecUnderTolerance = %+.2w
  Inverted = false
  LineAngle = 0
  LockPosition = false
  MeasureType = 1
  OverTolerance = 0
  Rotation = 0
  ScaleType = 0
  TheoreticalExact = false
  Type = 4
  UnderTolerance = 0
  X = 29.5278
  Y = -13.4557
FEATURE [TechDraw::DrawViewDimension] Dimension009
  AngleOverride = false
  Arbitrary = false
  ArbitraryTolerances = false
  EqualTolerance = true
  ExtensionAngle = 0
  FormatSpec = R%.2w
  FormatSpecOverTolerance = %+.2w
  FormatSpecUnderTolerance = %+.2w
  Inverted = false
  LineAngle = 0
  LockPosition = false
  MeasureType = 1
  OverTolerance = 0
  Rotation = 0
  ScaleType = 0
  TheoreticalExact = false
  Type = 4
  UnderTolerance = 0
  X = -27.036
  Y = -17.5672
FEATURE [TechDraw::DrawViewDimension] Dimension011
  AngleOverride = false
  Arbitrary = false
  ArbitraryTolerances = false
  EqualTolerance = true
  ExtensionAngle = 0
  FormatSpec = %.2w
  FormatSpecOverTolerance = %+.2w
  FormatSpecUnderTolerance = %+.2w
  Inverted = false
  LineAngle = 0
  LockPosition = false
  MeasureType = 1
  OverTolerance = 0
  References2D = -> [ProjItem]
  Rotation = 0
  ScaleType = 0
  TheoreticalExact = false
  Type = 2
  UnderTolerance = 0
  X = -21.4187
  Y = -22.1411
FEATURE [TechDraw::DrawViewPart] View
  CoarseView = false
  Direction = (0,-1,0)
  Focus = 100
  HardHidden = false
  IsoCount = 0
  IsoHidden = false
  IsoVisible = false
  LockPosition = false
  Perspective = false
  Rotation = 0
  ScaleType = 0
  SeamHidden = false
  SeamVisible = true
  SmoothHidden = false
  SmoothVisible = true
  Source = -> [Sketch]
  X = 63.7349
  XDirection = (1,0,0)
  Y = 122.699
FEATURE [TechDraw::DrawViewDimension] Dimension013
  AngleOverride = false
  Arbitrary = false
  ArbitraryTolerances = false
  EqualTolerance = true
  ExtensionAngle = 0
  FormatSpec = R%.2w
  FormatSpecOverTolerance = %+.2w
  FormatSpecUnderTolerance = %+.2w
  Inverted = false
  LineAngle = 0
  LockPosition = false
  MeasureType = 1
  OverTolerance = 0
  References2D = -> [View]
  Rotation = 0
  ScaleType = 0
  TheoreticalExact = false
  Type = 4
  UnderTolerance = 0
  X = -14.5503
  Y = 19.0346
FEATURE [TechDraw::DrawViewDimension] Dimension015
  AngleOverride = false
  Arbitrary = false
  ArbitraryTolerances = false
  EqualTolerance = true
  ExtensionAngle = 0
  FormatSpec = %.2w
  FormatSpecOverTolerance = %+.2w
  FormatSpecUnderTolerance = %+.2w
  Inverted = false
  LineAngle = 0
  LockPosition = false
  MeasureType = 1
  OverTolerance = 0
  References2D = -> [View]
  Rotation = 0
  ScaleType = 0
  TheoreticalExact = false
  Type = 2
  UnderTolerance = 0
  X = -20.8031
  Y = -9.82734
FEATURE [TechDraw::DrawViewDimension] Dimension017
  AngleOverride = false
  Arbitrary = false
  ArbitraryTolerances = false
  EqualTolerance = true
  ExtensionAngle = 0
  FormatSpec = %.2w
  FormatSpecOverTolerance = %+.2w
  FormatSpecUnderTolerance = %+.2w
  Inverted = false
  LineAngle = 0
  LockPosition = false
  MeasureType = 1
  OverTolerance = 0
  Rotation = 0
  ScaleType = 0
  TheoreticalExact = false
  Type = 1
  UnderTolerance = 0
  X = 0.796866
  Y = -17.3927
FEATURE [TechDraw::DrawViewPart] View001
  CoarseView = false
  Direction = (0,0,-1)
  Focus = 100
  HardHidden = false
  IsoCount = 0
  IsoHidden = false
  IsoVisible = false
  LockPosition = false
  Perspective = false
  Rotation = 0
  ScaleType = 0
  SeamHidden = false
  SeamVisible = true
  SmoothHidden = false
  SmoothVisible = true
  Source = -> [Sketch003]
  X = -10
  XDirection = (0,1,0)
  Y = 0
FEATURE [TechDraw::DrawViewSection] SectionView  label="Section A-A' - A-A'"
  BaseView = -> ProjItem
  CoarseView = false
  CutSurfaceDisplay = 2
  Direction = (0,0,1)
  FileGeomPattern = <path>
  FileHatchPattern = <path>
  Focus = 100
  FuseBeforeCut = false
  HardHidden = false
  HatchScale = 1
  IsoCount = 0
  IsoHidden = false
  IsoVisible = false
  LockPosition = false
  NameGeomPattern = Diamond
  Perspective = false
  Rotation = 0
  ScaleType = 2
  SeamHidden = false
  SeamVisible = true
  SectionDirection = 3
  SectionNormal = (0,0,1)
  SectionOrigin = (33.64,0,-62)
  SectionSymbol = A-A'
  SmoothHidden = false
  SmoothVisible = true
  Source = -> [Pad001]
  X = -10
  XDirection = (0,-1,0)
  Y = 1.25
FEATURE [TechDraw::DrawViewDimension] Dimension019
  AngleOverride = false
  Arbitrary = false
  ArbitraryTolerances = false
  EqualTolerance = true
  ExtensionAngle = 0
  FormatSpec = %.2w
  FormatSpecOverTolerance = %+.2w
  FormatSpecUnderTolerance = %+.2w
  Inverted = false
  LineAngle = 0
  LockPosition = false
  MeasureType = 1
  OverTolerance = 0
  References2D = -> [View001]
  Rotation = 0
  ScaleType = 0
  TheoreticalExact = false
  Type = 2
  UnderTolerance = 0
  X = 32.4982
  Y = 2.5
FEATURE [TechDraw::DrawViewDimension] Dimension020
  AngleOverride = false
  Arbitrary = false
  ArbitraryTolerances = false
  EqualTolerance = true
  ExtensionAngle = 0
  FormatSpec = %.2w
  FormatSpecOverTolerance = %+.2w
  FormatSpecUnderTolerance = %+.2w
  Inverted = false
  LineAngle = 0
  LockPosition = false
  MeasureType = 1
  OverTolerance = 0
  References2D = -> [View001]
  Rotation = 0
  ScaleType = 0
  TheoreticalExact = false
  Type = 1
  UnderTolerance = 0
  X = 0
  Y = -15.6629
FEATURE [TechDraw::DrawViewDimension] Dimension021
  AngleOverride = false
  Arbitrary = false
  ArbitraryTolerances = false
  EqualTolerance = true
  ExtensionAngle = 0
  FormatSpec = R%.2w
  FormatSpecOverTolerance = %+.2w
  FormatSpecUnderTolerance = %+.2w
  Inverted = false
  LineAngle = 0
  LockPosition = false
  MeasureType = 1
  OverTolerance = 0
  References2D = -> [View001]
  Rotation = 0
  ScaleType = 0
  TheoreticalExact = false
  Type = 4
  UnderTolerance = 0
  X = -21.2665
  Y = 28.4219
FEATURE [TechDraw::DrawViewDimension] Dimension022
  AngleOverride = false
  Arbitrary = false
  ArbitraryTolerances = false
  EqualTolerance = true
  ExtensionAngle = 0
  FormatSpec = %.2w
  FormatSpecOverTolerance = %+.2w
  FormatSpecUnderTolerance = %+.2w
  Inverted = false
  LineAngle = 0
  LockPosition = false
  MeasureType = 1
  OverTolerance = 0
  Rotation = 0
  ScaleType = 0
  TheoreticalExact = false
  Type = 2
  UnderTolerance = 0
  X = -26.9701
  Y = -0.340734
FEATURE [TechDraw::DrawViewDimension] Dimension023
  AngleOverride = false
  Arbitrary = false
  ArbitraryTolerances = false
  EqualTolerance = true
  ExtensionAngle = 0
  FormatSpec = %.2w
  FormatSpecOverTolerance = %+.2w
  FormatSpecUnderTolerance = %+.2w
  Inverted = false
  LineAngle = 0
  LockPosition = false
  MeasureType = 1
  OverTolerance = 0
  References2D = -> [SectionView]
  Rotation = 0
  ScaleType = 0
  TheoreticalExact = false
  Type = 1
  UnderTolerance = 0
  X = 22.0288
  Y = 19.6934
FEATURE [TechDraw::DrawViewDimension] Dimension026
  AngleOverride = false
  Arbitrary = false
  ArbitraryTolerances = false
  EqualTolerance = true
  ExtensionAngle = 0
  FormatSpec = %.2w
  FormatSpecOverTolerance = %+.2w
  FormatSpecUnderTolerance = %+.2w
  Inverted = false
  LineAngle = 0
  LockPosition = false
  MeasureType = 1
  OverTolerance = 0
  References2D = -> [SectionView]
  Rotation = 0
  ScaleType = 0
  TheoreticalExact = false
  Type = 2
  UnderTolerance = 0
  X = 24.8194
  Y = -17.1682
FEATURE [TechDraw::DrawViewDimension] Dimension027
  AngleOverride = false
  Arbitrary = false
  ArbitraryTolerances = false
  EqualTolerance = true
  ExtensionAngle = 0
  FormatSpec = %.2w
  FormatSpecOverTolerance = %+.2w
  FormatSpecUnderTolerance = %+.2w
  Inverted = false
  LineAngle = 0
  LockPosition = false
  MeasureType = 1
  OverTolerance = 0
  References2D = -> [SectionView]
  Rotation = 0
  ScaleType = 0
  TheoreticalExact = false
  Type = 2
  UnderTolerance = 0
  X = 25.2725
  Y = 23.7407
FEATURE [TechDraw::DrawViewSection] SectionView001  label="Section B-B' - B-B'"
  BaseView = -> ProjItem
  CoarseView = false
  CutSurfaceDisplay = 2
  Direction = (0,0,1)
  FileGeomPattern = <path>
  FileHatchPattern = <path>
  Focus = 100
  FuseBeforeCut = false
  HardHidden = false
  HatchScale = 1
  IsoCount = 0
  IsoHidden = false
  IsoVisible = false
  LockPosition = false
  NameGeomPattern = Diamond
  Perspective = false
  Rotation = 0
  ScaleType = 2
  SeamHidden = false
  SeamVisible = true
  SectionDirection = 3
  SectionNormal = (0,0,1)
  SectionOrigin = (50,0,-57.99)
  SectionSymbol = B-B'
  SmoothHidden = false
  SmoothVisible = true
  Source = -> [Pad001]
  X = 108.026
  XDirection = (0,-1,0)
  Y = 46.8055
FEATURE [TechDraw::DrawViewDimension] Dimension028
  AngleOverride = false
  Arbitrary = false
  ArbitraryTolerances = false
  EqualTolerance = true
  ExtensionAngle = 0
  FormatSpec = %.2w
  FormatSpecOverTolerance = %+.2w
  FormatSpecUnderTolerance = %+.2w
  Inverted = false
  LineAngle = 0
  LockPosition = false
  MeasureType = 1
  OverTolerance = 0
  References2D = -> [SectionView]
  Rotation = 0
  ScaleType = 0
  TheoreticalExact = false
  Type = 1
  UnderTolerance = 0
  X = 1.07646
  Y = 19.6402
FEATURE [TechDraw::DrawViewDimension] Dimension029
  AngleOverride = false
  Arbitrary = false
  ArbitraryTolerances = false
  EqualTolerance = true
  ExtensionAngle = 0
  FormatSpec = %.2w
  FormatSpecOverTolerance = %+.2w
  FormatSpecUnderTolerance = %+.2w
  Inverted = false
  LineAngle = 0
  LockPosition = false
  MeasureType = 1
  OverTolerance = 0
  References2D = -> [SectionView]
  Rotation = 0
  ScaleType = 0
  TheoreticalExact = false
  Type = 2
  UnderTolerance = 0
  X = 24.8793
  Y = 3.21764
FEATURE [TechDraw::DrawViewDimension] Dimension030
  AngleOverride = false
  Arbitrary = false
  ArbitraryTolerances = false
  EqualTolerance = true
  ExtensionAngle = 0
  FormatSpec = R%.2w
  FormatSpecOverTolerance = %+.2w
  FormatSpecUnderTolerance = %+.2w
  Inverted = false
  LineAngle = 0
  LockPosition = false
  MeasureType = 1
  OverTolerance = 0
  References2D = -> [SectionView]
  Rotation = 0
  ScaleType = 0
  TheoreticalExact = false
  Type = 4
  UnderTolerance = 0
  X = -24.918
  Y = -12.3344
FEATURE [TechDraw::DrawLeaderLine] LeaderLine
  AutoHorizontal = false
  EndSymbol = 7
  LeaderParent = -> ProjItem
  LockPosition = true
  Rotation = 0
  Scalable = true
  ScaleType = 0
  StartSymbol = 0
  WayPoints = (2) [(0,0,0),(-1.2459,-142.689,0)]
  X = -31.5406
  Y = -34.0836
FEATURE [TechDraw::DrawLeaderLine] LeaderLine001
  AutoHorizontal = false
  EndSymbol = 7
  LeaderParent = -> ProjItem
  LockPosition = true
  Rotation = 0
  Scalable = false
  ScaleType = 0
  StartSymbol = 0
  WayPoints = (2) [(0,0,0),(2.27374e-13,-135.301,0)]
  X = 31.5039
  Y = -33.9582
FEATURE [TechDraw::DrawLeaderLine] LeaderLine002
  AutoHorizontal = false
  EndSymbol = 7
  LeaderParent = -> ProjItem
  LockPosition = true
  Rotation = 0
  Scalable = false
  ScaleType = 0
  StartSymbol = 0
  WayPoints = (2) [(0,0,0),(1.2459,-135.803,0)]
  X = 25.7096
  Y = -32.1564
FEATURE [TechDraw::DrawLeaderLine] LeaderLine003
  AutoHorizontal = false
  EndSymbol = 7
  LeaderParent = -> ProjItem
  LockPosition = true
  Rotation = 0
  Scalable = false
  ScaleType = 0
  StartSymbol = 0
  WayPoints = (2) [(0,0,0),(2.4918,-135.146,0)]
  X = -25.4969
  Y = -32.0318
FEATURE [TechDraw::DrawViewAnnotation] Annotation
  Font = osifont
  LineSpace = 80
  LockPosition = false
  MaxWidth = -1
  Rotation = 0
  ScaleType = 0
  Text = A
  TextSize = 5
  TextStyle = 0
  X = 132.932
  Y = 106.774
FEATURE [TechDraw::DrawViewAnnotation] Annotation001
  Font = osifont
  LineSpace = 80
  LockPosition = false
  MaxWidth = -1
  Rotation = 0
  ScaleType = 0
  Text = A'
  TextSize = 5
  TextStyle = 0
  X = 196.969
  Y = 107.884
FEATURE [TechDraw::DrawViewAnnotation] Annotation002
  Font = osifont
  LineSpace = 80
  LockPosition = false
  MaxWidth = -1
  Rotation = 0
  ScaleType = 0
  Text = B
  TextSize = 5
  TextStyle = 0
  X = 139.56
  Y = 108.287
FEATURE [TechDraw::DrawViewAnnotation] Annotation003
  Font = osifont
  LineSpace = 80
  LockPosition = false
  MaxWidth = -1
  Rotation = 0
  ScaleType = 0
  Text = B'
  TextSize = 5
  TextStyle = 0
  X = 191.023
  Y = 107.684
FEATURE [TechDraw::DrawViewAnnotation] Annotation004
  Font = osifont
  LineSpace = 80
  LockPosition = false
  MaxWidth = -1
  Rotation = 0
  ScaleType = 0
  Text = Sección A - A'
  TextSize = 5
  TextStyle = 0
  X = -4.95497
  Y = 24.3792
FEATURE [TechDraw::DrawViewClip] Clip
  Height = 60
  LockPosition = false
  Rotation = 0
  ScaleType = 0
  ShowFrame = false
  Views = -> [View001,SectionView,Annotation004]
  Width = 80
  X = 50.8986
  Y = 45.3634
FEATURE [TechDraw::DrawViewDimension] Dimension032
  AngleOverride = false
  Arbitrary = false
  ArbitraryTolerances = false
  EqualTolerance = true
  ExtensionAngle = 0
  FormatSpec = %.2w
  FormatSpecOverTolerance = %+.2w
  FormatSpecUnderTolerance = %+.2w
  Inverted = false
  LineAngle = 0
  LockPosition = false
  MeasureType = 1
  OverTolerance = 0
  References2D = -> [SectionView001]
  Rotation = 0
  ScaleType = 0
  TheoreticalExact = false
  Type = 1
  UnderTolerance = 0
  X = -1.19606
  Y = 29.4364
FEATURE [TechDraw::DrawViewDimension] Dimension033
  AngleOverride = false
  Arbitrary = false
  ArbitraryTolerances = false
  EqualTolerance = true
  ExtensionAngle = 0
  FormatSpec = %.2w
  FormatSpecOverTolerance = %+.2w
  FormatSpecUnderTolerance = %+.2w
  Inverted = false
  LineAngle = 0
  LockPosition = false
  MeasureType = 1
  OverTolerance = 0
  References2D = -> [SectionView001]
  Rotation = 0
  ScaleType = 0
  TheoreticalExact = false
  Type = 2
  UnderTolerance = 0
  X = 21.7223
  Y = 1.60292
FEATURE [TechDraw::DrawViewDimension] Dimension034
  AngleOverride = false
  Arbitrary = false
  ArbitraryTolerances = false
  EqualTolerance = true
  ExtensionAngle = 0
  FormatSpec = R%.2w
  FormatSpecOverTolerance = %+.2w
  FormatSpecUnderTolerance = %+.2w
  Inverted = false
  LineAngle = 0
  LockPosition = false
  MeasureType = 1
  OverTolerance = 0
  References2D = -> [SectionView001]
  Rotation = 0
  ScaleType = 0
  TheoreticalExact = false
  Type = 4
  UnderTolerance = 0
  X = 25.8649
  Y = 23.3233
FEATURE [TechDraw::DrawViewAnnotation] Annotation005
  Font = osifont
  LineSpace = 80
  LockPosition = false
  MaxWidth = -1
  Rotation = 0
  ScaleType = 0
  Text = Sección B - B'
  TextSize = 5
  TextStyle = 0
  X = 108.255
  Y = 26.1662
FEATURE [TechDraw::DrawViewSection] SectionView002  label="Section C-C' - C-C'"
  BaseView = -> ProjItem
  CoarseView = false
  CutSurfaceDisplay = 2
  Direction = (0,0,1)
  FileGeomPattern = <path>
  FileHatchPattern = <path>
  Focus = 100
  FuseBeforeCut = false
  HardHidden = false
  HatchScale = 1
  IsoCount = 0
  IsoHidden = false
  IsoVisible = false
  LockPosition = false
  NameGeomPattern = Diamond
  Perspective = false
  Rotation = 0
  ScaleType = 0
  SeamHidden = false
  SeamVisible = true
  SectionDirection = 3
  SectionNormal = (0,0,1)
  SectionOrigin = (33.64,0,-24.75)
  SectionSymbol = C-C'
  SmoothHidden = false
  SmoothVisible = true
  Source = -> [Pad001]
  X = 211.416
  XDirection = (0,-1,0)
  Y = 62.8805
FEATURE [TechDraw::DrawLeaderLine] LeaderLine004
  AutoHorizontal = false
  EndSymbol = 7
  LeaderParent = -> ProjItem
  LockPosition = true
  Rotation = 0
  Scalable = false
  ScaleType = 0
  StartSymbol = 0
  WayPoints = (2) [(0,0,0),(-0.641399,-150.769,0)]
  X = -23.3235
  Y = 3.27079
FEATURE [TechDraw::DrawLeaderLine] LeaderLine005
  AutoHorizontal = false
  EndSymbol = 7
  LeaderParent = -> ProjItem
  LockPosition = true
  Rotation = 0
  Scalable = false
  ScaleType = 0
  StartSymbol = 0
  WayPoints = (2) [(0,0,0),(-2.0765,-157.814,0)]
  X = 22.8808
  Y = 3.11265
FEATURE [TechDraw::DrawViewAnnotation] Annotation006
  Font = osifont
  LineSpace = 80
  LockPosition = false
  MaxWidth = -1
  Rotation = 0
  ScaleType = 0
  Text = C
  TextSize = 5
  TextStyle = 0
  X = 141.008
  Y = 145.819
FEATURE [TechDraw::DrawViewAnnotation] Annotation007
  Font = osifont
  LineSpace = 80
  LockPosition = false
  MaxWidth = -1
  Rotation = 0
  ScaleType = 0
  Text = C'
  TextSize = 5
  TextStyle = 0
  X = 187.511
  Y = 147.369
FEATURE [TechDraw::DrawViewDimension] Dimension036
  AngleOverride = false
  Arbitrary = false
  ArbitraryTolerances = false
  EqualTolerance = true
  ExtensionAngle = 0
  FormatSpec = %.2w
  FormatSpecOverTolerance = %+.2w
  FormatSpecUnderTolerance = %+.2w
  Inverted = false
  LineAngle = 0
  LockPosition = false
  MeasureType = 1
  OverTolerance = 0
  References2D = -> [SectionView002]
  Rotation = 0
  ScaleType = 0
  TheoreticalExact = false
  Type = 2
  UnderTolerance = 0
  X = -25.9039
  Y = 2.00867
FEATURE [TechDraw::DrawViewDimension] Dimension037
  AngleOverride = false
  Arbitrary = false
  ArbitraryTolerances = false
  EqualTolerance = true
  ExtensionAngle = 0
  FormatSpec = %.2w
  FormatSpecOverTolerance = %+.2w
  FormatSpecUnderTolerance = %+.2w
  Inverted = false
  LineAngle = 0
  LockPosition = false
  MeasureType = 1
  OverTolerance = 0
  References2D = -> [SectionView002]
  Rotation = 0
  ScaleType = 0
  TheoreticalExact = false
  Type = 1
  UnderTolerance = 0
  X = -0.818889
  Y = 20.7834
FEATURE [TechDraw::DrawViewDimension] Dimension038
  AngleOverride = false
  Arbitrary = false
  ArbitraryTolerances = false
  EqualTolerance = true
  ExtensionAngle = 0
  FormatSpec = %.2w
  FormatSpecOverTolerance = %+.2w
  FormatSpecUnderTolerance = %+.2w
  Inverted = false
  LineAngle = 0
  LockPosition = false
  MeasureType = 1
  OverTolerance = 0
  References2D = -> [SectionView002]
  Rotation = 0
  ScaleType = 0
  TheoreticalExact = false
  Type = 1
  UnderTolerance = 0
  X = -0.163778
  Y = -13.8181
FEATURE [TechDraw::DrawViewDimension] Dimension039
  AngleOverride = false
  Arbitrary = false
  ArbitraryTolerances = false
  EqualTolerance = true
  ExtensionAngle = 0
  FormatSpec = %.2w
  FormatSpecOverTolerance = %+.2w
  FormatSpecUnderTolerance = %+.2w
  Inverted = false
  LineAngle = 0
  LockPosition = false
  MeasureType = 1
  OverTolerance = 0
  References2D = -> [SectionView002]
  Rotation = 0
  ScaleType = 0
  TheoreticalExact = false
  Type = 2
  UnderTolerance = 0
  X = 21.9921
  Y = 2.49999
FEATURE [TechDraw::DrawViewDimension] Dimension040
  AngleOverride = false
  Arbitrary = false
  ArbitraryTolerances = false
  EqualTolerance = true
  ExtensionAngle = 0
  FormatSpec = R%.2w
  FormatSpecOverTolerance = %+.2w
  FormatSpecUnderTolerance = %+.2w
  Inverted = false
  LineAngle = 0
  LockPosition = false
  MeasureType = 1
  OverTolerance = 0
  References2D = -> [SectionView002]
  Rotation = 0
  ScaleType = 0
  TheoreticalExact = false
  Type = 4
  UnderTolerance = 0
  X = 25.2218
  Y = 18.0156
FEATURE [TechDraw::DrawViewDimension] Dimension041
  AngleOverride = false
  Arbitrary = false
  ArbitraryTolerances = false
  EqualTolerance = true
  ExtensionAngle = 0
  FormatSpec = R%.2w
  FormatSpecOverTolerance = %+.2w
  FormatSpecUnderTolerance = %+.2w
  Inverted = false
  LineAngle = 0
  LockPosition = false
  MeasureType = 1
  OverTolerance = 0
  References2D = -> [SectionView002]
  Rotation = 0
  ScaleType = 0
  TheoreticalExact = false
  Type = 4
  UnderTolerance = 0
  X = -28.4973
  Y = -13.266
FEATURE [TechDraw::DrawViewAnnotation] Annotation008
  Font = osifont
  LineSpace = 80
  LockPosition = false
  MaxWidth = -1
  Rotation = 0
  ScaleType = 0
  Text = Sección C - C'
  TextSize = 5
  TextStyle = 0
  X = 172.273
  Y = 69.6806
FEATURE [Sketcher::SketchObject] Sketch017
  FullyConstrained = false
  MapMode = 5
  Placement = pos=(24.7487,0,-1.5365e-12) rot=(0.678598,0.678598,0.281085;2.59356rad)
  Support = -> [DatumPlane]
  sketch-geometry (7):
    g0: LineSegment StartX=-30.1513 StartY=-12.499 StartZ=0 EndX=-30.1513 EndY=-54.7653 EndZ=0
    g1: LineSegment StartX=-30.1513 StartY=-54.7653 StartZ=0 EndX=24.5327 EndY=-54.7653 EndZ=0
    g2: LineSegment StartX=24.5327 StartY=-54.7653 StartZ=0 EndX=24.5327 EndY=-13.699 EndZ=0
    g3: ArcOfCircle CenterX=-20.9483 CenterY=-6.91791 CenterZ=0 NormalX=0 NormalY=0 NormalZ=1 AngleXU=0 Radius=10.7631 StartAngle=3.68674 EndAngle=5.34684
    g4: ArcOfCircle CenterX=-3.81614 CenterY=-30.1968 CenterZ=0 NormalX=0 NormalY=0 NormalZ=1 AngleXU=0 Radius=18.1405 StartAngle=1.11508 EndAngle=2.20525
    g5: ArcOfCircle CenterX=29.6965 CenterY=38.1791 CenterZ=0 NormalX=0 NormalY=0 NormalZ=1 AngleXU=0 Radius=58.0065 StartAngle=4.25667 EndAngle=4.46144
    g6: ArcOfCircle CenterX=17.2873 CenterY=-10.2282 CenterZ=0 NormalX=0 NormalY=0 NormalZ=1 AngleXU=0 Radius=8.03387 StartAngle=4.46144 EndAngle=5.83645
  constraints (10):
    c: Coincident(g0,g1)
    c: Coincident(g1,g2)
    c: Horizontal(g1)
    c: Vertical(g0)
    c: Vertical(g2)
    c: Coincident(g3,g0)
    c: Coincident(g6,g2)
    c: Tangent(g6,g5) = -1.5708
    c: Tangent(g5,g4) = 1.5708
    c: Tangent(g4,g3) = 1.5708
FEATURE [PartDesign::Pocket] Pocket005
  BaseFeature = -> Pad001
  Direction = (-0.707107,-2e-16,0.707107)
  Length = 5
  Length2 = 5
  Placement = pos=(24.7487,0,-1.537e-12) rot=(0.678598,0.678598,0.281085;2.59356rad)
  Profile = -> Sketch017
  ReferenceAxis = -> Sketch017 [N_Axis]
  Reversed = true
  Type = 1
FEATURE [TechDraw::DrawViewPart] View002
  CoarseView = false
  Direction = (-0.707,0,0.707)
  Focus = 100
  HardHidden = false
  IsoCount = 0
  IsoHidden = false
  IsoVisible = false
  LockPosition = false
  Perspective = false
  Rotation = 0
  ScaleType = 0
  SeamHidden = false
  SeamVisible = true
  SmoothHidden = false
  SmoothVisible = true
  Source = -> [Pocket005,Sketch006,Sketch001]
  X = 115.063
  XDirection = (0,-1,0)
  Y = 160.189
FEATURE [TechDraw::DrawViewBalloon] Balloon
  BubbleShape = 0
  EndType = 0
  EndTypeScale = 1
  KinkLength = 5
  LockPosition = false
  OriginX = -12
  OriginY = 28
  Rotation = 0
  ScaleType = 0
  ShapeScale = 1
  SourceView = -> ProjItem001
  Text = D
  TextWrapLen = -1
  X = -40.6797
  Y = 43.7717
FEATURE [TechDraw::DrawViewDimension] Dimension043
  AngleOverride = false
  Arbitrary = false
  ArbitraryTolerances = false
  EqualTolerance = true
  ExtensionAngle = 0
  FormatSpec = %.2w
  FormatSpecOverTolerance = %+.2w
  FormatSpecUnderTolerance = %+.2w
  Inverted = false
  LineAngle = 0
  LockPosition = false
  MeasureType = 1
  OverTolerance = 0
  References2D = -> [View002]
  Rotation = 0
  ScaleType = 0
  TheoreticalExact = false
  Type = 1
  UnderTolerance = 0
  X = 0.187326
  Y = -10.9781
FEATURE [TechDraw::DrawViewDimension] Dimension044
  AngleOverride = false
  Arbitrary = false
  ArbitraryTolerances = false
  EqualTolerance = true
  ExtensionAngle = 0
  FormatSpec = %.2w
  FormatSpecOverTolerance = %+.2w
  FormatSpecUnderTolerance = %+.2w
  Inverted = false
  LineAngle = 0
  LockPosition = false
  MeasureType = 1
  OverTolerance = 0
  References2D = -> [View002]
  Rotation = 0
  ScaleType = 0
  TheoreticalExact = false
  Type = 2
  UnderTolerance = 0
  X = -22.0739
  Y = 6.68722
FEATURE [TechDraw::DrawViewDimension] Dimension045
  AngleOverride = false
  Arbitrary = false
  ArbitraryTolerances = false
  EqualTolerance = true
  ExtensionAngle = 0
  FormatSpec = %.2w
  FormatSpecOverTolerance = %+.2w
  FormatSpecUnderTolerance = %+.2w
  Inverted = false
  LineAngle = 0
  LockPosition = false
  MeasureType = 1
  OverTolerance = 0
  References2D = -> [View002]
  Rotation = 0
  ScaleType = 0
  TheoreticalExact = false
  Type = 1
  UnderTolerance = 0
  X = 0.608513
  Y = 22.6996
FEATURE [TechDraw::DrawViewDimension] Dimension046
  AngleOverride = false
  Arbitrary = false
  ArbitraryTolerances = false
  EqualTolerance = true
  ExtensionAngle = 0
  FormatSpec = %.2w
  FormatSpecOverTolerance = %+.2w
  FormatSpecUnderTolerance = %+.2w
  Inverted = false
  LineAngle = 0
  LockPosition = false
  MeasureType = 1
  OverTolerance = 0
  References2D = -> [View002]
  Rotation = 0
  ScaleType = 0
  TheoreticalExact = false
  Type = 2
  UnderTolerance = 0
  X = 19.3986
  Y = 7.69768
FEATURE [TechDraw::DrawViewAnnotation] Annotation009
  Font = osifont
  LineSpace = 80
  LockPosition = false
  MaxWidth = -1
  Rotation = 0
  ScaleType = 0
  Text = Vista D
  TextSize = 5
  TextStyle = 0
  X = 115.845
  Y = 184.754
FEATURE [TechDraw::DrawViewDimension] Dimension048
  AngleOverride = false
  Arbitrary = false
  ArbitraryTolerances = false
  EqualTolerance = true
  ExtensionAngle = 0
  FormatSpec = ⌀%.2w
  FormatSpecOverTolerance = %+.2w
  FormatSpecUnderTolerance = %+.2w
  Inverted = false
  LineAngle = 0
  LockPosition = false
  MeasureType = 1
  OverTolerance = 0
  References2D = -> [ProjItem001]
  Rotation = 0
  ScaleType = 0
  TheoreticalExact = false
  Type = 5
  UnderTolerance = 0
  X = -33.219
  Y = 19.8092
FEATURE [TechDraw::DrawViewSymbol] Symbol
  LockPosition = false
  Rotation = 0
  Scale = 0.3
  ScaleType = 2
  Symbol = <blob: 2444 chars omitted>
  X = 217.487
  Y = 36.9001
FEATURE [TechDraw::DrawViewDimension] Dimension055
  AngleOverride = false
  Arbitrary = false
  ArbitraryTolerances = false
  EqualTolerance = true
  ExtensionAngle = 0
  FormatSpec = R%.2w
  FormatSpecOverTolerance = %+.2w
  FormatSpecUnderTolerance = %+.2w
  Inverted = false
  LineAngle = 0
  LockPosition = false
  MeasureType = 1
  OverTolerance = 0
  References2D = -> [SectionView001]
  Rotation = 0
  ScaleType = 0
  TheoreticalExact = false
  Type = 4
  UnderTolerance = 0
  X = 30.2689
  Y = -15.2433
FEATURE [TechDraw::DrawViewDimension] Dimension057
  AngleOverride = false
  Arbitrary = false
  ArbitraryTolerances = false
  EqualTolerance = true
  ExtensionAngle = 0
  FormatSpec = %.2w
  FormatSpecOverTolerance = %+.2w
  FormatSpecUnderTolerance = %+.2w
  Inverted = false
  LineAngle = 0
  LockPosition = false
  MeasureType = 1
  OverTolerance = 0
  References2D = -> [SectionView001]
  Rotation = 0
  ScaleType = 0
  TheoreticalExact = false
  Type = 2
  UnderTolerance = 0
  X = -27.1162
  Y = -4.09938
FEATURE [TechDraw::DrawViewDimension] Dimension058
  AngleOverride = false
  Arbitrary = false
  ArbitraryTolerances = false
  EqualTolerance = true
  ExtensionAngle = 0
  FormatSpec = %.2w
  FormatSpecOverTolerance = %+.2w
  FormatSpecUnderTolerance = %+.2w
  Inverted = false
  LineAngle = 0
  LockPosition = false
  MeasureType = 1
  OverTolerance = 0
  References2D = -> [SectionView001]
  Rotation = 0
  ScaleType = 0
  TheoreticalExact = false
  Type = 1
  UnderTolerance = 0
  X = 2.19831
  Y = 23.6831
FEATURE [TechDraw::DrawViewDimension] Dimension059
  AngleOverride = false
  Arbitrary = false
  ArbitraryTolerances = false
  EqualTolerance = true
  ExtensionAngle = 0
  FormatSpec = ⌀%.2w
  FormatSpecOverTolerance = %+.2w
  FormatSpecUnderTolerance = %+.2w
  Inverted = false
  LineAngle = 0
  LockPosition = false
  MeasureType = 1
  OverTolerance = 0
  References2D = -> [SectionView001]
  Rotation = 0
  ScaleType = 0
  TheoreticalExact = false
  Type = 5
  UnderTolerance = 0
  X = -2.76095
  Y = -4.14142
FEATURE [TechDraw::DrawViewDimension] Dimension061
  AngleOverride = false
  Arbitrary = false
  ArbitraryTolerances = false
  EqualTolerance = true
  ExtensionAngle = 0
  FormatSpec = R%.2w
  FormatSpecOverTolerance = %+.2w
  FormatSpecUnderTolerance = %+.2w
  Inverted = false
  LineAngle = 0
  LockPosition = false
  MeasureType = 1
  OverTolerance = 0
  References2D = -> [ProjItem001]
  Rotation = 0
  ScaleType = 0
  TheoreticalExact = false
  Type = 4
  UnderTolerance = 0
  X = -16.5471
  Y = 50.3249
FEATURE [TechDraw::DrawViewDimension] Dimension063
  AngleOverride = false
  Arbitrary = false
  ArbitraryTolerances = false
  EqualTolerance = true
  ExtensionAngle = 0
  FormatSpec = %.2w
  FormatSpecOverTolerance = %+.2w
  FormatSpecUnderTolerance = %+.2w
  Inverted = false
  LineAngle = 0
  LockPosition = false
  MeasureType = 1
  OverTolerance = 0
  References2D = -> [ProjItem001]
  Rotation = 0
  ScaleType = 0
  TheoreticalExact = false
  Type = 2
  UnderTolerance = 0
  X = 20.9902
  Y = 13.6016
FEATURE [TechDraw::DrawViewDimension] Dimension064
  AngleOverride = false
  Arbitrary = false
  ArbitraryTolerances = false
  EqualTolerance = true
  ExtensionAngle = 0
  FormatSpec = %.2w
  FormatSpecOverTolerance = %+.2w
  FormatSpecUnderTolerance = %+.2w
  Inverted = false
  LineAngle = 0
  LockPosition = false
  MeasureType = 1
  OverTolerance = 0
  References2D = -> [ProjItem001]
  Rotation = 0
  ScaleType = 0
  TheoreticalExact = false
  Type = 1
  UnderTolerance = 0
  X = -25.5875
  Y = 8.66094
FEATURE [Sketcher::SketchObject] Sketch018
  FullyConstrained = false
  MapMode = 5
  Placement = pos=(19.4965,2.85578,10.0836) rot=(0.287968,0.287968,0.913318;1.66134rad)
  Support = -> [DatumPlane005]
  sketch-geometry (5):
    g0: Circle CenterX=-3.08556 CenterY=-10.2888 CenterZ=0 NormalX=0 NormalY=0 NormalZ=1 AngleXU=0 Radius=15.9107
    g1: LineSegment StartX=-36.4417 StartY=21.8986 StartZ=0 EndX=34.2023 EndY=21.8986 EndZ=0
    g2: LineSegment StartX=34.2023 StartY=21.8986 StartZ=0 EndX=34.2023 EndY=-72.0163 EndZ=0
    g3: LineSegment StartX=34.2023 StartY=-72.0163 StartZ=0 EndX=-36.4417 EndY=-72.0163 EndZ=0
    g4: LineSegment StartX=-36.4417 StartY=-72.0163 StartZ=0 EndX=-36.4417 EndY=21.8986 EndZ=0
  constraints (8):
    c: Coincident(g1,g2)
    c: Coincident(g2,g3)
    c: Coincident(g3,g4)
    c: Coincident(g4,g1)
    c: Horizontal(g1)
    c: Horizontal(g3)
    c: Vertical(g2)
    c: Vertical(g4)
FEATURE [PartDesign::Pocket] Pocket006
  BaseFeature = -> Pocket005
  Direction = (-0.573576,-1.4e-15,-0.819152)
  Length = 5
  Length2 = 5
  Placement = pos=(24.7487,0,-1.537e-12) rot=(0.678598,0.678598,0.281085;2.59356rad)
  Profile = -> Sketch018
  ReferenceAxis = -> Sketch018 [N_Axis]
  Type = 1
FEATURE [PartDesign::Body] Body
  Group = -> [Sketch,DatumPlane,Sketch001,DatumPlane001,Sketch002,DatumPlane002,Sketch003,AdditivePipe,Sketch004,Pocket,Sketch006,Sketch007,DatumPlane003,Sketch008,Sketch009,SubtractivePipe,DatumPlane004,Sketch010,Pocket001,Sketch011,Pocket002,Fillet,Sketch012,DatumPlane005,Sketch013,Pad,Fillet001,Fillet002,Fillet003,Sketch014,Pocket003,Sketch015,Pocket004,Sketch016,Pad001,Sketch017,Pocket005,Sketch018,+1 more]
  Origin = -> Origin
  Tip = -> Pocket006
FEATURE [TechDraw::DrawViewPart] View003
  CoarseView = false
  Direction = (0.574,0,0.819)
  Focus = 100
  HardHidden = false
  IsoCount = 0
  IsoHidden = false
  IsoVisible = false
  LockPosition = false
  Perspective = false
  Rotation = 0
  ScaleType = 0
  SeamHidden = false
  SeamVisible = true
  SmoothHidden = false
  SmoothVisible = true
  Source = -> [Pocket006,Sketch013]
  X = 212.543
  XDirection = (0,1,0)
  Y = 163.991
FEATURE [TechDraw::DrawViewBalloon] Balloon001
  BubbleShape = 0
  EndType = 0
  EndTypeScale = 1
  KinkLength = 5
  LockPosition = false
  OriginX = -3.68362
  OriginY = 33.2684
  Rotation = 0
  ScaleType = 0
  ShapeScale = 1
  SourceView = -> ProjItem001
  Text = E
  TextWrapLen = -1
  X = 13.3346
  Y = 40.5128
FEATURE [TechDraw::DrawViewDimension] Dimension067
  AngleOverride = false
  Arbitrary = false
  ArbitraryTolerances = false
  EqualTolerance = true
  ExtensionAngle = 0
  FormatSpec = R%.2w
  FormatSpecOverTolerance = %+.2w
  FormatSpecUnderTolerance = %+.2w
  Inverted = false
  LineAngle = 0
  LockPosition = false
  MeasureType = 1
  OverTolerance = 0
  References2D = -> [View003]
  Rotation = 0
  ScaleType = 0
  TheoreticalExact = false
  Type = 4
  UnderTolerance = 0
  X = 16.365
  Y = 19.7781
FEATURE [TechDraw::DrawViewDimension] Dimension068
  AngleOverride = false
  Arbitrary = false
  ArbitraryTolerances = false
  EqualTolerance = true
  ExtensionAngle = 0
  FormatSpec = %.2w
  FormatSpecOverTolerance = %+.2w
  FormatSpecUnderTolerance = %+.2w
  Inverted = false
  LineAngle = 0
  LockPosition = false
  MeasureType = 1
  OverTolerance = 0
  References2D = -> [View003]
  Rotation = 0
  ScaleType = 0
  TheoreticalExact = false
  Type = 1
  UnderTolerance = 0
  X = -8.8728
  Y = 20.431
FEATURE [TechDraw::DrawViewDimension] Dimension069
  AngleOverride = false
  Arbitrary = false
  ArbitraryTolerances = false
  EqualTolerance = true
  ExtensionAngle = 0
  FormatSpec = %.2w
  FormatSpecOverTolerance = %+.2w
  FormatSpecUnderTolerance = %+.2w
  Inverted = false
  LineAngle = 0
  LockPosition = false
  MeasureType = 1
  OverTolerance = 0
  References2D = -> [View003]
  Rotation = 0
  ScaleType = 0
  TheoreticalExact = false
  Type = 1
  UnderTolerance = 0
  X = 0.084407
  Y = 3.75456
FEATURE [TechDraw::DrawViewAnnotation] Annotation010
  Font = osifont
  LineSpace = 80
  LockPosition = false
  MaxWidth = -1
  Rotation = 0
  ScaleType = 0
  Text = Vista E
  TextSize = 5
  TextStyle = 0
  X = 212.522
  Y = 188.098
FEATURE [TechDraw::DrawViewDimension] Dimension072
  AngleOverride = false
  Arbitrary = false
  ArbitraryTolerances = false
  EqualTolerance = true
  ExtensionAngle = 0
  FormatSpec = %.2w
  FormatSpecOverTolerance = %+.2w
  FormatSpecUnderTolerance = %+.2w
  Inverted = false
  LineAngle = 0
  LockPosition = false
  MeasureType = 1
  OverTolerance = 0
  References2D = -> [ProjItem001]
  Rotation = 0
  ScaleType = 0
  TheoreticalExact = false
  Type = 6
  UnderTolerance = 0
  X = 11.3418
  Y = 27.9763
FEATURE [TechDraw::DrawViewDimension] Dimension073
  AngleOverride = false
  Arbitrary = false
  ArbitraryTolerances = false
  EqualTolerance = true
  ExtensionAngle = 0
  FormatSpec = %.2w
  FormatSpecOverTolerance = %+.2w
  FormatSpecUnderTolerance = %+.2w
  Inverted = false
  LineAngle = 0
  LockPosition = false
  MeasureType = 1
  OverTolerance = 0
  References2D = -> [ProjItem001]
  Rotation = 0
  ScaleType = 0
  TheoreticalExact = false
  Type = 6
  UnderTolerance = 0
  X = -53.0542
  Y = 45.8711
FEATURE [TechDraw::DrawViewDimension] Dimension074
  AngleOverride = false
  Arbitrary = false
  ArbitraryTolerances = false
  EqualTolerance = true
  ExtensionAngle = 0
  FormatSpec = R%.2w
  FormatSpecOverTolerance = %+.2w
  FormatSpecUnderTolerance = %+.2w
  Inverted = false
  LineAngle = 0
  LockPosition = false
  MeasureType = 1
  OverTolerance = 0
  References2D = -> [ProjItem001]
  Rotation = 0
  ScaleType = 0
  TheoreticalExact = false
  Type = 4
  UnderTolerance = 0
  X = 3.78058
  Y = 50.5086
FEATURE [TechDraw::DrawViewDimension] Dimension075
  AngleOverride = false
  Arbitrary = false
  ArbitraryTolerances = false
  EqualTolerance = true
  ExtensionAngle = 0
  FormatSpec = %.2w
  FormatSpecOverTolerance = %+.2w
  FormatSpecUnderTolerance = %+.2w
  Inverted = false
  LineAngle = 0
  LockPosition = false
  MeasureType = 1
  OverTolerance = 0
  References2D = -> [ProjItem001]
  Rotation = 0
  ScaleType = 0
  TheoreticalExact = false
  Type = 0
  UnderTolerance = 0
  X = -29.0049
  Y = 53.9979
FEATURE [TechDraw::DrawViewDimension] Dimension076
  AngleOverride = false
  Arbitrary = false
  ArbitraryTolerances = false
  EqualTolerance = true
  ExtensionAngle = 0
  FormatSpec = %.2w
  FormatSpecOverTolerance = %+.2w
  FormatSpecUnderTolerance = %+.2w
  Inverted = false
  LineAngle = 0
  LockPosition = false
  MeasureType = 1
  OverTolerance = 0
  References2D = -> [View003]
  Rotation = 0
  ScaleType = 0
  TheoreticalExact = false
  Type = 2
  UnderTolerance = 0
  X = -20.7671
  Y = 16.1629
FEATURE [TechDraw::DrawViewDimension] Dimension077
  AngleOverride = false
  Arbitrary = false
  ArbitraryTolerances = false
  EqualTolerance = true
  ExtensionAngle = 0
  FormatSpec = R%.2w
  FormatSpecOverTolerance = %+.2w
  FormatSpecUnderTolerance = %+.2w
  Inverted = false
  LineAngle = 0
  LockPosition = false
  MeasureType = 1
  OverTolerance = 0
  References2D = -> [ProjItem001]
  Rotation = 0
  ScaleType = 0
  TheoreticalExact = false
  Type = 4
  UnderTolerance = 0
  X = -30.3497
  Y = 30.8748
FEATURE [TechDraw::DrawViewDimension] Dimension078
  AngleOverride = false
  Arbitrary = false
  ArbitraryTolerances = false
  EqualTolerance = true
  ExtensionAngle = 0
  FormatSpec = %.2w
  FormatSpecOverTolerance = %+.2w
  FormatSpecUnderTolerance = %+.2w
  Inverted = false
  LineAngle = 0
  LockPosition = false
  MeasureType = 1
  OverTolerance = 0
  References2D = -> [ProjItem002]
  Rotation = 0
  ScaleType = 0
  TheoreticalExact = false
  Type = 2
  UnderTolerance = 0
  X = 23.6132
  Y = -31.6524
FEATURE [TechDraw::DrawPage] Page003  label="Boquilla"
  KeepUpdated = true
  NextBalloonIndex = 3
  ProjectionType = 0
  Template = -> Template003
  Views = -> [ProjGroup,Dimension,Dimension001,Dimension002,Dimension003,Dimension004,Dimension008,Dimension009,Dimension011,View,Dimension013,Dimension015,Dimension017,View001,SectionView,Dimension019,Dimension020,Dimension021,Dimension022,Dimension023,Dimension026,Dimension027,SectionView001,Dimension028,Dimension029,Dimension030,LeaderLine,LeaderLine001,LeaderLine002,LeaderLine003,Annotation,Annotation001,+49 more]
note: 6 file-system paths scrubbed to <path> (originals preserved in the JSON sidecar)
